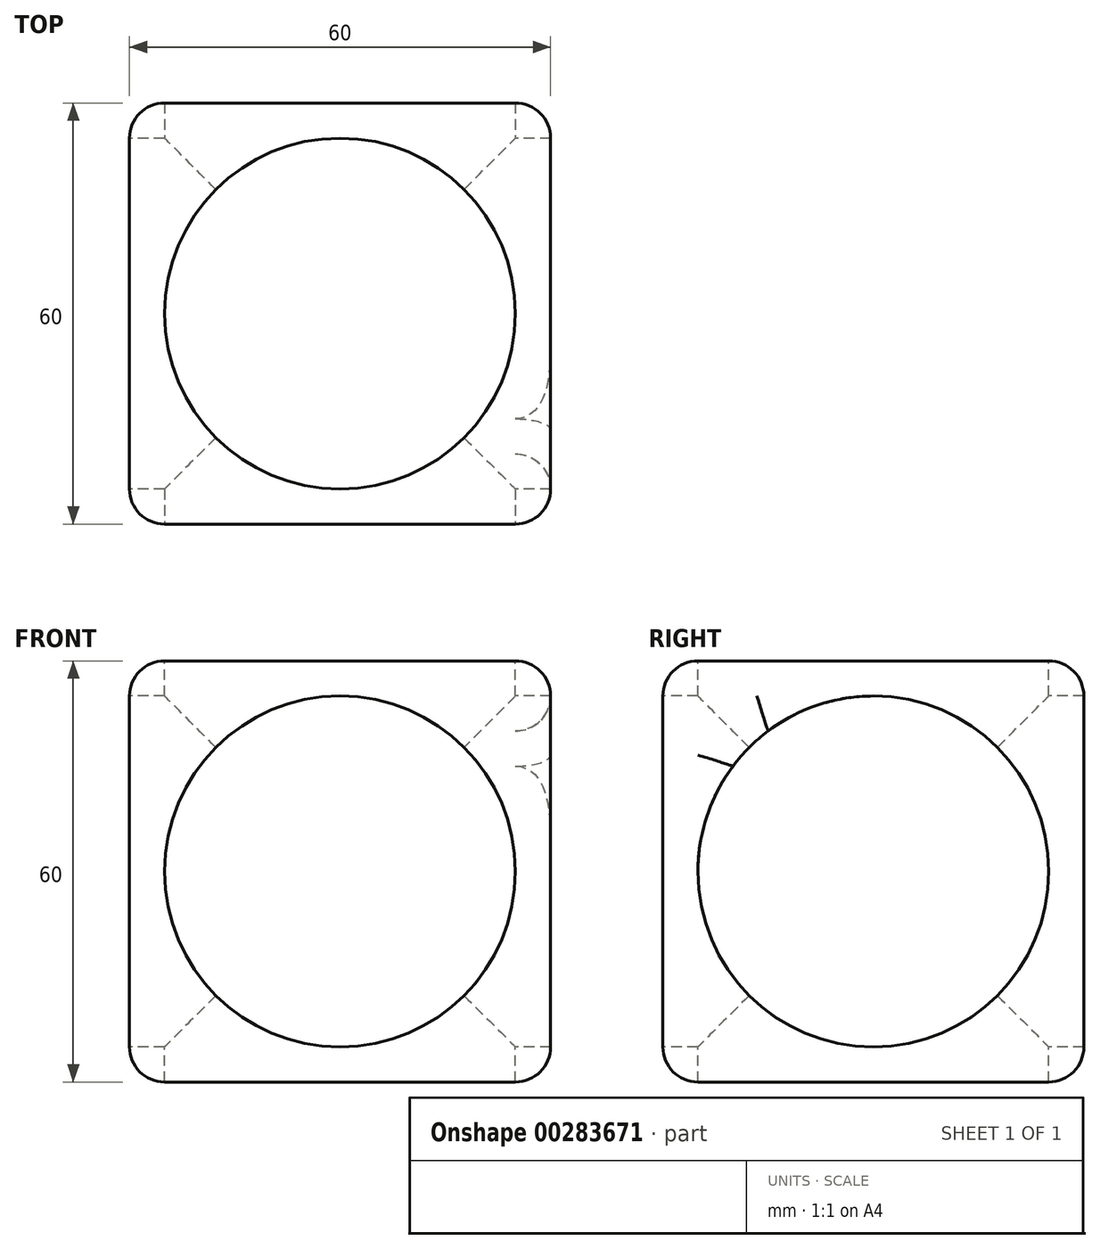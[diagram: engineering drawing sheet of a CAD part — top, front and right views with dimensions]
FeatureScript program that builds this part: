
annotation { "Feature Type Name" : "Feature", "Feature Type Description" : "" }
export const myFeature = defineFeature(function(context is Context, id is Id, definition is map)
    precondition{}
    {
        {
            var Q0;
            Q0=qCreatedBy(makeId("Top.planeOp"),FACE);
            var sketch = newSketch(context, id + "F0", { "sketchPlane" : qUnion([Q0])});
            skLineSegment(sketch, "E0.bottom", {"start": v(30, 30) * mm, "end": v(-30, 30) * mm});
            skLineSegment(sketch, "E0.top", {"start": v(30, -30) * mm, "end": v(-30, -30) * mm});
            skLineSegment(sketch, "E0.left", {"start": v(30, 30) * mm, "end": v(30, -30) * mm});
            skLineSegment(sketch, "E0.right", {"start": v(-30, 30) * mm, "end": v(-30, -30) * mm});
            skPoint(sketch, "E0.middle", {"position": v(0, 0) * mm});
            skSolve(sketch);
        }
        {
            var Q0;
            Q0=makeQuery(id+"F0.imprint","IMPRINT",FACE,{"disambiguationData":[TD([[makeQuery(id+"F0.imprint","IMPRINT",EDGE,{"derivedFrom":sQuery(id+"F0.wireOp",EDGE,"E0.bottom")}),1.0]])]});
            extrude(context, id + "F1", {"entities" : qUnion([Q0]), "depth" : 60 * mm});
        }
        {
            var Q0;
            Q0=makeQuery(id+"F1.opExtrude","CAP_FACE",FACE,{"disambiguationData":[OSD([sQuery(id+"F0.wireOp",EDGE,"E0.bottom"),sQuery(id+"F0.wireOp",EDGE,"E0.top"),sQuery(id+"F0.wireOp",EDGE,"E0.left"),sQuery(id+"F0.wireOp",EDGE,"E0.right")])],"isStart":false});
            var sketch = newSketch(context, id + "F2", { "sketchPlane" : qUnion([Q0])});
            skCircle(sketch, "E1", {"center": v(0, 0) * mm, "radius": 25 * mm});
            skSolve(sketch);
        }
        {
            var Q0;
            Q0=sQuery(id+"F2.wireOp",VERTEX,"E1.center");
            var Q1;
            Q1=makeQuery(id+"F1.opExtrude","SWEPT_BODY",BODY,{"disambiguationData":[OSD([sQuery(id+"F0.wireOp",EDGE,"E0.bottom"),sQuery(id+"F0.wireOp",EDGE,"E0.top"),sQuery(id+"F0.wireOp",EDGE,"E0.left"),sQuery(id+"F0.wireOp",EDGE,"E0.right")])]});
            hole(context, id + "F3", {"style" : HoleStyle.SIMPLE, "endStyle" : HoleEndStyle.THROUGH, "holeDiameter" : 50 * mm, "tappedDepth" : 12 * mm, "tapClearance" : 3, "locations" : qUnion([Q0]), "scope" : qUnion([Q1])});
        }
        {
            var Q0;
            Q0=makeQuery(id+"F1.opExtrude","SWEPT_FACE",FACE,{"disambiguationData":[OSD([sQuery(id+"F0.wireOp",EDGE,"E0.right")])]});
            var sketch = newSketch(context, id + "F4", { "sketchPlane" : qUnion([Q0])});
            skCircle(sketch, "E2", {"center": v(0, 30) * mm, "radius": 30 * mm});
            skPoint(sketch, "E2.first.point", {"position": v(0, 60) * mm});
            skPoint(sketch, "E2.second.point", {"position": v(30, 30) * mm});
            skPoint(sketch, "E2.third.point", {"position": v(-30, 30) * mm});
            skSolve(sketch);
        }
        {
            var Q0;
            Q0=sQuery(id+"F4.wireOp",VERTEX,"E2.center");
            var Q1;
            Q1=makeQuery(id+"F1.opExtrude","SWEPT_BODY",BODY,{"disambiguationData":[OSD([sQuery(id+"F0.wireOp",EDGE,"E0.bottom"),sQuery(id+"F0.wireOp",EDGE,"E0.top"),sQuery(id+"F0.wireOp",EDGE,"E0.left"),sQuery(id+"F0.wireOp",EDGE,"E0.right")])]});
            hole(context, id + "F5", {"style" : HoleStyle.SIMPLE, "endStyle" : HoleEndStyle.THROUGH, "holeDiameter" : 50 * mm, "tappedDepth" : 12 * mm, "tapClearance" : 3, "locations" : qUnion([Q0]), "scope" : qUnion([Q1])});
        }
        {
            var Q0;
            Q0=makeQuery(id+"F1.opExtrude","SWEPT_FACE",FACE,{"disambiguationData":[OSD([sQuery(id+"F0.wireOp",EDGE,"E0.top")])]});
            var sketch = newSketch(context, id + "F6", { "sketchPlane" : qUnion([Q0])});
            skCircle(sketch, "E3", {"center": v(0, 30) * mm, "radius": 30 * mm});
            skPoint(sketch, "E3.first.point", {"position": v(0, 60) * mm});
            skPoint(sketch, "E3.second.point", {"position": v(30, 30) * mm});
            skPoint(sketch, "E3.third.point", {"position": v(-30, 30) * mm});
            skSolve(sketch);
        }
        {
            var Q0;
            Q0=sQuery(id+"F6.wireOp",VERTEX,"E3.center");
            var Q1;
            Q1=makeQuery(id+"F1.opExtrude","SWEPT_BODY",BODY,{"disambiguationData":[OSD([sQuery(id+"F0.wireOp",EDGE,"E0.bottom"),sQuery(id+"F0.wireOp",EDGE,"E0.top"),sQuery(id+"F0.wireOp",EDGE,"E0.left"),sQuery(id+"F0.wireOp",EDGE,"E0.right")])]});
            hole(context, id + "F7", {"style" : HoleStyle.SIMPLE, "endStyle" : HoleEndStyle.THROUGH, "holeDiameter" : 50 * mm, "tappedDepth" : 12 * mm, "tapClearance" : 3, "locations" : qUnion([Q0]), "scope" : qUnion([Q1])});
        }
        {
            var Q0;
            Q0=makeQuery(id+"F1.opExtrude","CAP_EDGE",EDGE,{"disambiguationData":[OSD([sQuery(id+"F0.wireOp",EDGE,"E0.bottom")])],"isStart":false});
            var Q1;
            Q1=makeQuery(id+"F1.opExtrude","CAP_EDGE",EDGE,{"disambiguationData":[OSD([sQuery(id+"F0.wireOp",EDGE,"E0.left")])],"isStart":false});
            var Q2;
            Q2=makeQuery(id+"F1.opExtrude","SWEPT_EDGE",EDGE,{"disambiguationData":[OSD([sQuery(id+"F0.wireOp",EDGE,"E0.bottom"),sQuery(id+"F0.wireOp",EDGE,"E0.left")])]});
            var Q3;
            Q3=makeQuery(id+"F1.opExtrude","CAP_EDGE",EDGE,{"disambiguationData":[OSD([sQuery(id+"F0.wireOp",EDGE,"E0.bottom")])],"isStart":true});
            var Q4;
            Q4=makeQuery(id+"F1.opExtrude","CAP_EDGE",EDGE,{"disambiguationData":[OSD([sQuery(id+"F0.wireOp",EDGE,"E0.left")])],"isStart":true});
            var Q5;
            Q5=makeQuery(id+"F1.opExtrude","SWEPT_EDGE",EDGE,{"disambiguationData":[OSD([sQuery(id+"F0.wireOp",EDGE,"E0.top"),sQuery(id+"F0.wireOp",EDGE,"E0.left")])]});
            var Q6;
            Q6=makeQuery(id+"F1.opExtrude","CAP_EDGE",EDGE,{"disambiguationData":[OSD([sQuery(id+"F0.wireOp",EDGE,"E0.right")])],"isStart":true});
            var Q7;
            Q7=makeQuery(id+"F1.opExtrude","CAP_EDGE",EDGE,{"disambiguationData":[OSD([sQuery(id+"F0.wireOp",EDGE,"E0.top")])],"isStart":true});
            var Q8;
            Q8=makeQuery(id+"F1.opExtrude","SWEPT_EDGE",EDGE,{"disambiguationData":[OSD([sQuery(id+"F0.wireOp",EDGE,"E0.top"),sQuery(id+"F0.wireOp",EDGE,"E0.right")])]});
            var Q9;
            Q9=makeQuery(id+"F1.opExtrude","CAP_EDGE",EDGE,{"disambiguationData":[OSD([sQuery(id+"F0.wireOp",EDGE,"E0.top")])],"isStart":false});
            var Q10;
            Q10=makeQuery(id+"F1.opExtrude","CAP_EDGE",EDGE,{"disambiguationData":[OSD([sQuery(id+"F0.wireOp",EDGE,"E0.right")])],"isStart":false});
            var Q11;
            Q11=makeQuery(id+"F1.opExtrude","SWEPT_EDGE",EDGE,{"disambiguationData":[OSD([sQuery(id+"F0.wireOp",EDGE,"E0.bottom"),sQuery(id+"F0.wireOp",EDGE,"E0.right")])]});
            fillet(context, id + "F8", {"entities" : qUnion([Q0, Q1, Q2, Q3, Q4, Q5, Q6, Q7, Q8, Q9, Q10, Q11]), "radius" : 5 * mm, "tangentPropagation" : true, "allowEdgeOverflow" : false});
        }
        {
            var Q0;
            Q0=makeQuery(id+"F5.hole-0.boolean.opBoolean","INTERSECT",EDGE,{"derivedFrom":[makeQuery(id+"F1.opExtrude","SWEPT_FACE",FACE,{"disambiguationData":[OSD([sQuery(id+"F0.wireOp",EDGE,"E0.left")])]}),makeQuery(id+"F5.hole-0.opRevolve","SWEPT_FACE",FACE,{"disambiguationData":[OSD([sQuery(id+"F5.hole-0.sketch.wireOp",EDGE,"core_line_2")])]})]});
            var Q1;
            Q1=makeQuery(id+"F5.hole-0.boolean.opBoolean","INTERSECT",EDGE,{"derivedFrom":[makeQuery(id+"F1.opExtrude","SWEPT_FACE",FACE,{"disambiguationData":[OSD([sQuery(id+"F0.wireOp",EDGE,"E0.left")])]}),makeQuery(id+"F5.hole-0.opRevolve","SWEPT_FACE",FACE,{"disambiguationData":[OSD([sQuery(id+"F5.hole-0.sketch.wireOp",EDGE,"core_line_2")])]})]});
            var Q2;
            Q2=makeQuery(id+"F5.hole-0.boolean.opBoolean","INTERSECT",EDGE,{"derivedFrom":[makeQuery(id+"F1.opExtrude","SWEPT_FACE",FACE,{"disambiguationData":[OSD([sQuery(id+"F0.wireOp",EDGE,"E0.left")])]}),makeQuery(id+"F5.hole-0.opRevolve","SWEPT_FACE",FACE,{"disambiguationData":[OSD([sQuery(id+"F5.hole-0.sketch.wireOp",EDGE,"core_line_2")])]})]});
            var Q3;
            Q3=makeQuery(id+"F5.hole-0.boolean.opBoolean","INTERSECT",EDGE,{"derivedFrom":[makeQuery(id+"F1.opExtrude","SWEPT_FACE",FACE,{"disambiguationData":[OSD([sQuery(id+"F0.wireOp",EDGE,"E0.left")])]}),makeQuery(id+"F5.hole-0.opRevolve","SWEPT_FACE",FACE,{"disambiguationData":[OSD([sQuery(id+"F5.hole-0.sketch.wireOp",EDGE,"core_line_2")])]})]});
            var Q4;
            Q4=makeQuery(id+"F5.hole-0.boolean.opBoolean","INTERSECT",EDGE,{"derivedFrom":[makeQuery(id+"F1.opExtrude","SWEPT_FACE",FACE,{"disambiguationData":[OSD([sQuery(id+"F0.wireOp",EDGE,"E0.left")])]}),makeQuery(id+"F5.hole-0.opRevolve","SWEPT_FACE",FACE,{"disambiguationData":[OSD([sQuery(id+"F5.hole-0.sketch.wireOp",EDGE,"core_line_2")])]})]});
            var Q5;
            Q5=makeQuery(id+"F5.hole-0.boolean.opBoolean","INTERSECT",EDGE,{"derivedFrom":[makeQuery(id+"F1.opExtrude","SWEPT_FACE",FACE,{"disambiguationData":[OSD([sQuery(id+"F0.wireOp",EDGE,"E0.left")])]}),makeQuery(id+"F5.hole-0.opRevolve","SWEPT_FACE",FACE,{"disambiguationData":[OSD([sQuery(id+"F5.hole-0.sketch.wireOp",EDGE,"core_line_2")])]})]});
            var Q6;
            Q6=makeQuery(id+"F5.hole-0.boolean.opBoolean","INTERSECT",EDGE,{"derivedFrom":[makeQuery(id+"F1.opExtrude","SWEPT_FACE",FACE,{"disambiguationData":[OSD([sQuery(id+"F0.wireOp",EDGE,"E0.left")])]}),makeQuery(id+"F5.hole-0.opRevolve","SWEPT_FACE",FACE,{"disambiguationData":[OSD([sQuery(id+"F5.hole-0.sketch.wireOp",EDGE,"core_line_2")])]})]});
            var Q7;
            Q7=makeQuery(id+"F5.hole-0.boolean.opBoolean","INTERSECT",EDGE,{"derivedFrom":[makeQuery(id+"F1.opExtrude","SWEPT_FACE",FACE,{"disambiguationData":[OSD([sQuery(id+"F0.wireOp",EDGE,"E0.left")])]}),makeQuery(id+"F5.hole-0.opRevolve","SWEPT_FACE",FACE,{"disambiguationData":[OSD([sQuery(id+"F5.hole-0.sketch.wireOp",EDGE,"core_line_2")])]})]});
            var Q8;
            Q8=makeQuery(id+"F5.hole-0.boolean.opBoolean","INTERSECT",EDGE,{"derivedFrom":[makeQuery(id+"F1.opExtrude","SWEPT_FACE",FACE,{"disambiguationData":[OSD([sQuery(id+"F0.wireOp",EDGE,"E0.left")])]}),makeQuery(id+"F5.hole-0.opRevolve","SWEPT_FACE",FACE,{"disambiguationData":[OSD([sQuery(id+"F5.hole-0.sketch.wireOp",EDGE,"core_line_2")])]})]});
            var Q9;
            Q9=makeQuery(id+"F5.hole-0.boolean.opBoolean","INTERSECT",EDGE,{"derivedFrom":[makeQuery(id+"F1.opExtrude","SWEPT_FACE",FACE,{"disambiguationData":[OSD([sQuery(id+"F0.wireOp",EDGE,"E0.left")])]}),makeQuery(id+"F5.hole-0.opRevolve","SWEPT_FACE",FACE,{"disambiguationData":[OSD([sQuery(id+"F5.hole-0.sketch.wireOp",EDGE,"core_line_2")])]})]});
            var Q10;
            Q10=makeQuery(id+"F5.hole-0.boolean.opBoolean","INTERSECT",EDGE,{"derivedFrom":[makeQuery(id+"F1.opExtrude","SWEPT_FACE",FACE,{"disambiguationData":[OSD([sQuery(id+"F0.wireOp",EDGE,"E0.left")])]}),makeQuery(id+"F5.hole-0.opRevolve","SWEPT_FACE",FACE,{"disambiguationData":[OSD([sQuery(id+"F5.hole-0.sketch.wireOp",EDGE,"core_line_2")])]})]});
            var Q11;
            Q11=makeQuery(id+"F5.hole-0.boolean.opBoolean","INTERSECT",EDGE,{"derivedFrom":[makeQuery(id+"F1.opExtrude","SWEPT_FACE",FACE,{"disambiguationData":[OSD([sQuery(id+"F0.wireOp",EDGE,"E0.left")])]}),makeQuery(id+"F5.hole-0.opRevolve","SWEPT_FACE",FACE,{"disambiguationData":[OSD([sQuery(id+"F5.hole-0.sketch.wireOp",EDGE,"core_line_2")])]})]});
            var Q12;
            Q12=makeQuery(id+"F5.hole-0.boolean.opBoolean","INTERSECT",EDGE,{"derivedFrom":[makeQuery(id+"F1.opExtrude","SWEPT_FACE",FACE,{"disambiguationData":[OSD([sQuery(id+"F0.wireOp",EDGE,"E0.left")])]}),makeQuery(id+"F5.hole-0.opRevolve","SWEPT_FACE",FACE,{"disambiguationData":[OSD([sQuery(id+"F5.hole-0.sketch.wireOp",EDGE,"core_line_2")])]})]});
            var Q13;
            Q13=makeQuery(id+"F5.hole-0.boolean.opBoolean","INTERSECT",EDGE,{"derivedFrom":[makeQuery(id+"F1.opExtrude","SWEPT_FACE",FACE,{"disambiguationData":[OSD([sQuery(id+"F0.wireOp",EDGE,"E0.left")])]}),makeQuery(id+"F5.hole-0.opRevolve","SWEPT_FACE",FACE,{"disambiguationData":[OSD([sQuery(id+"F5.hole-0.sketch.wireOp",EDGE,"core_line_2")])]})]});
            var Q14;
            Q14=makeQuery(id+"F5.hole-0.boolean.opBoolean","INTERSECT",EDGE,{"derivedFrom":[makeQuery(id+"F1.opExtrude","SWEPT_FACE",FACE,{"disambiguationData":[OSD([sQuery(id+"F0.wireOp",EDGE,"E0.left")])]}),makeQuery(id+"F5.hole-0.opRevolve","SWEPT_FACE",FACE,{"disambiguationData":[OSD([sQuery(id+"F5.hole-0.sketch.wireOp",EDGE,"core_line_2")])]})]});
            var Q15;
            Q15=makeQuery(id+"F5.hole-0.boolean.opBoolean","INTERSECT",EDGE,{"derivedFrom":[makeQuery(id+"F1.opExtrude","SWEPT_FACE",FACE,{"disambiguationData":[OSD([sQuery(id+"F0.wireOp",EDGE,"E0.left")])]}),makeQuery(id+"F5.hole-0.opRevolve","SWEPT_FACE",FACE,{"disambiguationData":[OSD([sQuery(id+"F5.hole-0.sketch.wireOp",EDGE,"core_line_2")])]})]});
            var Q16;
            Q16=makeQuery(id+"F5.hole-0.boolean.opBoolean","INTERSECT",EDGE,{"derivedFrom":[makeQuery(id+"F1.opExtrude","SWEPT_FACE",FACE,{"disambiguationData":[OSD([sQuery(id+"F0.wireOp",EDGE,"E0.left")])]}),makeQuery(id+"F5.hole-0.opRevolve","SWEPT_FACE",FACE,{"disambiguationData":[OSD([sQuery(id+"F5.hole-0.sketch.wireOp",EDGE,"core_line_2")])]})]});
            var Q17;
            Q17=makeQuery(id+"F5.hole-0.boolean.opBoolean","INTERSECT",EDGE,{"derivedFrom":[makeQuery(id+"F1.opExtrude","SWEPT_FACE",FACE,{"disambiguationData":[OSD([sQuery(id+"F0.wireOp",EDGE,"E0.left")])]}),makeQuery(id+"F5.hole-0.opRevolve","SWEPT_FACE",FACE,{"disambiguationData":[OSD([sQuery(id+"F5.hole-0.sketch.wireOp",EDGE,"core_line_2")])]})]});
            var Q18;
            Q18=makeQuery(id+"F5.hole-0.boolean.opBoolean","INTERSECT",EDGE,{"derivedFrom":[makeQuery(id+"F1.opExtrude","SWEPT_FACE",FACE,{"disambiguationData":[OSD([sQuery(id+"F0.wireOp",EDGE,"E0.left")])]}),makeQuery(id+"F5.hole-0.opRevolve","SWEPT_FACE",FACE,{"disambiguationData":[OSD([sQuery(id+"F5.hole-0.sketch.wireOp",EDGE,"core_line_2")])]})]});
            var Q19;
            Q19=makeQuery(id+"F5.hole-0.boolean.opBoolean","INTERSECT",EDGE,{"derivedFrom":[makeQuery(id+"F1.opExtrude","SWEPT_FACE",FACE,{"disambiguationData":[OSD([sQuery(id+"F0.wireOp",EDGE,"E0.left")])]}),makeQuery(id+"F5.hole-0.opRevolve","SWEPT_FACE",FACE,{"disambiguationData":[OSD([sQuery(id+"F5.hole-0.sketch.wireOp",EDGE,"core_line_2")])]})]});
            var Q20;
            Q20=makeQuery(id+"F5.hole-0.boolean.opBoolean","INTERSECT",EDGE,{"derivedFrom":[makeQuery(id+"F1.opExtrude","SWEPT_FACE",FACE,{"disambiguationData":[OSD([sQuery(id+"F0.wireOp",EDGE,"E0.left")])]}),makeQuery(id+"F5.hole-0.opRevolve","SWEPT_FACE",FACE,{"disambiguationData":[OSD([sQuery(id+"F5.hole-0.sketch.wireOp",EDGE,"core_line_2")])]})]});
            var Q21;
            Q21=makeQuery(id+"F5.hole-0.boolean.opBoolean","INTERSECT",EDGE,{"derivedFrom":[makeQuery(id+"F1.opExtrude","SWEPT_FACE",FACE,{"disambiguationData":[OSD([sQuery(id+"F0.wireOp",EDGE,"E0.left")])]}),makeQuery(id+"F5.hole-0.opRevolve","SWEPT_FACE",FACE,{"disambiguationData":[OSD([sQuery(id+"F5.hole-0.sketch.wireOp",EDGE,"core_line_2")])]})]});
            var Q22;
            Q22=makeQuery(id+"F5.hole-0.boolean.opBoolean","INTERSECT",EDGE,{"derivedFrom":[makeQuery(id+"F1.opExtrude","SWEPT_FACE",FACE,{"disambiguationData":[OSD([sQuery(id+"F0.wireOp",EDGE,"E0.left")])]}),makeQuery(id+"F5.hole-0.opRevolve","SWEPT_FACE",FACE,{"disambiguationData":[OSD([sQuery(id+"F5.hole-0.sketch.wireOp",EDGE,"core_line_2")])]})]});
            var Q23;
            Q23=makeQuery(id+"F5.hole-0.boolean.opBoolean","INTERSECT",EDGE,{"derivedFrom":[makeQuery(id+"F1.opExtrude","SWEPT_FACE",FACE,{"disambiguationData":[OSD([sQuery(id+"F0.wireOp",EDGE,"E0.left")])]}),makeQuery(id+"F5.hole-0.opRevolve","SWEPT_FACE",FACE,{"disambiguationData":[OSD([sQuery(id+"F5.hole-0.sketch.wireOp",EDGE,"core_line_2")])]})]});
            var Q24;
            Q24=makeQuery(id+"F5.hole-0.boolean.opBoolean","INTERSECT",EDGE,{"derivedFrom":[makeQuery(id+"F1.opExtrude","SWEPT_FACE",FACE,{"disambiguationData":[OSD([sQuery(id+"F0.wireOp",EDGE,"E0.left")])]}),makeQuery(id+"F5.hole-0.opRevolve","SWEPT_FACE",FACE,{"disambiguationData":[OSD([sQuery(id+"F5.hole-0.sketch.wireOp",EDGE,"core_line_2")])]})]});
            var Q25;
            Q25=makeQuery(id+"F5.hole-0.boolean.opBoolean","INTERSECT",EDGE,{"derivedFrom":[makeQuery(id+"F1.opExtrude","SWEPT_FACE",FACE,{"disambiguationData":[OSD([sQuery(id+"F0.wireOp",EDGE,"E0.left")])]}),makeQuery(id+"F5.hole-0.opRevolve","SWEPT_FACE",FACE,{"disambiguationData":[OSD([sQuery(id+"F5.hole-0.sketch.wireOp",EDGE,"core_line_2")])]})]});
            var Q26;
            Q26=makeQuery(id+"F5.hole-0.boolean.opBoolean","INTERSECT",EDGE,{"derivedFrom":[makeQuery(id+"F1.opExtrude","SWEPT_FACE",FACE,{"disambiguationData":[OSD([sQuery(id+"F0.wireOp",EDGE,"E0.left")])]}),makeQuery(id+"F5.hole-0.opRevolve","SWEPT_FACE",FACE,{"disambiguationData":[OSD([sQuery(id+"F5.hole-0.sketch.wireOp",EDGE,"core_line_2")])]})]});
            var Q27;
            Q27=makeQuery(id+"F5.hole-0.boolean.opBoolean","INTERSECT",EDGE,{"derivedFrom":[makeQuery(id+"F1.opExtrude","SWEPT_FACE",FACE,{"disambiguationData":[OSD([sQuery(id+"F0.wireOp",EDGE,"E0.left")])]}),makeQuery(id+"F5.hole-0.opRevolve","SWEPT_FACE",FACE,{"disambiguationData":[OSD([sQuery(id+"F5.hole-0.sketch.wireOp",EDGE,"core_line_2")])]})]});
            var Q28;
            Q28=makeQuery(id+"F5.hole-0.boolean.opBoolean","INTERSECT",EDGE,{"derivedFrom":[makeQuery(id+"F1.opExtrude","SWEPT_FACE",FACE,{"disambiguationData":[OSD([sQuery(id+"F0.wireOp",EDGE,"E0.left")])]}),makeQuery(id+"F5.hole-0.opRevolve","SWEPT_FACE",FACE,{"disambiguationData":[OSD([sQuery(id+"F5.hole-0.sketch.wireOp",EDGE,"core_line_2")])]})]});
            var Q29;
            Q29=makeQuery(id+"F5.hole-0.boolean.opBoolean","INTERSECT",EDGE,{"derivedFrom":[makeQuery(id+"F1.opExtrude","SWEPT_FACE",FACE,{"disambiguationData":[OSD([sQuery(id+"F0.wireOp",EDGE,"E0.left")])]}),makeQuery(id+"F5.hole-0.opRevolve","SWEPT_FACE",FACE,{"disambiguationData":[OSD([sQuery(id+"F5.hole-0.sketch.wireOp",EDGE,"core_line_2")])]})]});
            var Q30;
            Q30=makeQuery(id+"F5.hole-0.boolean.opBoolean","INTERSECT",EDGE,{"derivedFrom":[makeQuery(id+"F1.opExtrude","SWEPT_FACE",FACE,{"disambiguationData":[OSD([sQuery(id+"F0.wireOp",EDGE,"E0.left")])]}),makeQuery(id+"F5.hole-0.opRevolve","SWEPT_FACE",FACE,{"disambiguationData":[OSD([sQuery(id+"F5.hole-0.sketch.wireOp",EDGE,"core_line_2")])]})]});
            var Q31;
            Q31=makeQuery(id+"F5.hole-0.boolean.opBoolean","INTERSECT",EDGE,{"derivedFrom":[makeQuery(id+"F1.opExtrude","SWEPT_FACE",FACE,{"disambiguationData":[OSD([sQuery(id+"F0.wireOp",EDGE,"E0.left")])]}),makeQuery(id+"F5.hole-0.opRevolve","SWEPT_FACE",FACE,{"disambiguationData":[OSD([sQuery(id+"F5.hole-0.sketch.wireOp",EDGE,"core_line_2")])]})]});
            var Q32;
            Q32=makeQuery(id+"F5.hole-0.boolean.opBoolean","INTERSECT",EDGE,{"derivedFrom":[makeQuery(id+"F1.opExtrude","SWEPT_FACE",FACE,{"disambiguationData":[OSD([sQuery(id+"F0.wireOp",EDGE,"E0.left")])]}),makeQuery(id+"F5.hole-0.opRevolve","SWEPT_FACE",FACE,{"disambiguationData":[OSD([sQuery(id+"F5.hole-0.sketch.wireOp",EDGE,"core_line_2")])]})]});
            var Q33;
            Q33=makeQuery(id+"F5.hole-0.boolean.opBoolean","INTERSECT",EDGE,{"derivedFrom":[makeQuery(id+"F1.opExtrude","SWEPT_FACE",FACE,{"disambiguationData":[OSD([sQuery(id+"F0.wireOp",EDGE,"E0.left")])]}),makeQuery(id+"F5.hole-0.opRevolve","SWEPT_FACE",FACE,{"disambiguationData":[OSD([sQuery(id+"F5.hole-0.sketch.wireOp",EDGE,"core_line_2")])]})]});
            var Q34;
            Q34=makeQuery(id+"F5.hole-0.boolean.opBoolean","INTERSECT",EDGE,{"derivedFrom":[makeQuery(id+"F1.opExtrude","SWEPT_FACE",FACE,{"disambiguationData":[OSD([sQuery(id+"F0.wireOp",EDGE,"E0.left")])]}),makeQuery(id+"F5.hole-0.opRevolve","SWEPT_FACE",FACE,{"disambiguationData":[OSD([sQuery(id+"F5.hole-0.sketch.wireOp",EDGE,"core_line_2")])]})]});
            var Q35;
            Q35=makeQuery(id+"F5.hole-0.boolean.opBoolean","INTERSECT",EDGE,{"derivedFrom":[makeQuery(id+"F1.opExtrude","SWEPT_FACE",FACE,{"disambiguationData":[OSD([sQuery(id+"F0.wireOp",EDGE,"E0.left")])]}),makeQuery(id+"F5.hole-0.opRevolve","SWEPT_FACE",FACE,{"disambiguationData":[OSD([sQuery(id+"F5.hole-0.sketch.wireOp",EDGE,"core_line_2")])]})]});
            var Q36;
            Q36=makeQuery(id+"F5.hole-0.boolean.opBoolean","COPY",EDGE,{"derivedFrom":makeQuery(id+"F5.hole-0.opRevolve","SWEPT_EDGE",EDGE,{"disambiguationData":[OSD([sQuery(id+"F5.hole-0.sketch.wireOp",EDGE,"core_line_2"),sQuery(id+"F5.hole-0.sketch.wireOp",EDGE,"core_line_3")])]})});
            var Q37;
            Q37=makeQuery(id+"F5.hole-0.boolean.opBoolean","COPY",EDGE,{"derivedFrom":makeQuery(id+"F5.hole-0.opRevolve","SWEPT_EDGE",EDGE,{"disambiguationData":[OSD([sQuery(id+"F5.hole-0.sketch.wireOp",EDGE,"core_line_2"),sQuery(id+"F5.hole-0.sketch.wireOp",EDGE,"core_line_3")])]})});
            var Q38;
            Q38=makeQuery(id+"F5.hole-0.boolean.opBoolean","COPY",EDGE,{"derivedFrom":makeQuery(id+"F5.hole-0.opRevolve","SWEPT_EDGE",EDGE,{"disambiguationData":[OSD([sQuery(id+"F5.hole-0.sketch.wireOp",EDGE,"core_line_2"),sQuery(id+"F5.hole-0.sketch.wireOp",EDGE,"core_line_3")])]})});
            var Q39;
            Q39=makeQuery(id+"F5.hole-0.boolean.opBoolean","COPY",EDGE,{"derivedFrom":makeQuery(id+"F5.hole-0.opRevolve","SWEPT_EDGE",EDGE,{"disambiguationData":[OSD([sQuery(id+"F5.hole-0.sketch.wireOp",EDGE,"core_line_2"),sQuery(id+"F5.hole-0.sketch.wireOp",EDGE,"core_line_3")])]})});
            var Q40;
            Q40=makeQuery(id+"F5.hole-0.boolean.opBoolean","COPY",EDGE,{"derivedFrom":makeQuery(id+"F5.hole-0.opRevolve","SWEPT_EDGE",EDGE,{"disambiguationData":[OSD([sQuery(id+"F5.hole-0.sketch.wireOp",EDGE,"core_line_2"),sQuery(id+"F5.hole-0.sketch.wireOp",EDGE,"core_line_3")])]})});
            var Q41;
            Q41=makeQuery(id+"F5.hole-0.boolean.opBoolean","COPY",EDGE,{"derivedFrom":makeQuery(id+"F5.hole-0.opRevolve","SWEPT_EDGE",EDGE,{"disambiguationData":[OSD([sQuery(id+"F5.hole-0.sketch.wireOp",EDGE,"core_line_2"),sQuery(id+"F5.hole-0.sketch.wireOp",EDGE,"core_line_3")])]})});
            var Q42;
            Q42=makeQuery(id+"F5.hole-0.boolean.opBoolean","COPY",EDGE,{"derivedFrom":makeQuery(id+"F5.hole-0.opRevolve","SWEPT_EDGE",EDGE,{"disambiguationData":[OSD([sQuery(id+"F5.hole-0.sketch.wireOp",EDGE,"core_line_2"),sQuery(id+"F5.hole-0.sketch.wireOp",EDGE,"core_line_3")])]})});
            var Q43;
            Q43=makeQuery(id+"F5.hole-0.boolean.opBoolean","COPY",EDGE,{"derivedFrom":makeQuery(id+"F5.hole-0.opRevolve","SWEPT_EDGE",EDGE,{"disambiguationData":[OSD([sQuery(id+"F5.hole-0.sketch.wireOp",EDGE,"core_line_2"),sQuery(id+"F5.hole-0.sketch.wireOp",EDGE,"core_line_3")])]})});
            var Q44;
            Q44=makeQuery(id+"F5.hole-0.boolean.opBoolean","COPY",EDGE,{"derivedFrom":makeQuery(id+"F5.hole-0.opRevolve","SWEPT_EDGE",EDGE,{"disambiguationData":[OSD([sQuery(id+"F5.hole-0.sketch.wireOp",EDGE,"core_line_2"),sQuery(id+"F5.hole-0.sketch.wireOp",EDGE,"core_line_3")])]})});
            var Q45;
            Q45=makeQuery(id+"F5.hole-0.boolean.opBoolean","COPY",EDGE,{"derivedFrom":makeQuery(id+"F5.hole-0.opRevolve","SWEPT_EDGE",EDGE,{"disambiguationData":[OSD([sQuery(id+"F5.hole-0.sketch.wireOp",EDGE,"core_line_2"),sQuery(id+"F5.hole-0.sketch.wireOp",EDGE,"core_line_3")])]})});
            var Q46;
            Q46=makeQuery(id+"F5.hole-0.boolean.opBoolean","COPY",EDGE,{"derivedFrom":makeQuery(id+"F5.hole-0.opRevolve","SWEPT_EDGE",EDGE,{"disambiguationData":[OSD([sQuery(id+"F5.hole-0.sketch.wireOp",EDGE,"core_line_2"),sQuery(id+"F5.hole-0.sketch.wireOp",EDGE,"core_line_3")])]})});
            var Q47;
            Q47=makeQuery(id+"F5.hole-0.boolean.opBoolean","COPY",EDGE,{"derivedFrom":makeQuery(id+"F5.hole-0.opRevolve","SWEPT_EDGE",EDGE,{"disambiguationData":[OSD([sQuery(id+"F5.hole-0.sketch.wireOp",EDGE,"core_line_2"),sQuery(id+"F5.hole-0.sketch.wireOp",EDGE,"core_line_3")])]})});
            var Q48;
            Q48=makeQuery(id+"F5.hole-0.boolean.opBoolean","INTERSECT",EDGE,{"derivedFrom":[makeQuery(id+"F1.opExtrude","SWEPT_FACE",FACE,{"disambiguationData":[OSD([sQuery(id+"F0.wireOp",EDGE,"E0.left")])]}),makeQuery(id+"F5.hole-0.opRevolve","SWEPT_FACE",FACE,{"disambiguationData":[OSD([sQuery(id+"F5.hole-0.sketch.wireOp",EDGE,"core_line_2")])]})]});
            var Q49;
            Q49=makeQuery(id+"F5.hole-0.boolean.opBoolean","INTERSECT",EDGE,{"derivedFrom":[makeQuery(id+"F1.opExtrude","SWEPT_FACE",FACE,{"disambiguationData":[OSD([sQuery(id+"F0.wireOp",EDGE,"E0.left")])]}),makeQuery(id+"F5.hole-0.opRevolve","SWEPT_FACE",FACE,{"disambiguationData":[OSD([sQuery(id+"F5.hole-0.sketch.wireOp",EDGE,"core_line_2")])]})]});
            var Q50;
            Q50=makeQuery(id+"F5.hole-0.boolean.opBoolean","INTERSECT",EDGE,{"derivedFrom":[makeQuery(id+"F1.opExtrude","SWEPT_FACE",FACE,{"disambiguationData":[OSD([sQuery(id+"F0.wireOp",EDGE,"E0.left")])]}),makeQuery(id+"F5.hole-0.opRevolve","SWEPT_FACE",FACE,{"disambiguationData":[OSD([sQuery(id+"F5.hole-0.sketch.wireOp",EDGE,"core_line_2")])]})]});
            var Q51;
            Q51=makeQuery(id+"F5.hole-0.boolean.opBoolean","INTERSECT",EDGE,{"derivedFrom":[makeQuery(id+"F1.opExtrude","SWEPT_FACE",FACE,{"disambiguationData":[OSD([sQuery(id+"F0.wireOp",EDGE,"E0.left")])]}),makeQuery(id+"F5.hole-0.opRevolve","SWEPT_FACE",FACE,{"disambiguationData":[OSD([sQuery(id+"F5.hole-0.sketch.wireOp",EDGE,"core_line_2")])]})]});
            var Q52;
            Q52=makeQuery(id+"F5.hole-0.boolean.opBoolean","INTERSECT",EDGE,{"derivedFrom":[makeQuery(id+"F1.opExtrude","SWEPT_FACE",FACE,{"disambiguationData":[OSD([sQuery(id+"F0.wireOp",EDGE,"E0.left")])]}),makeQuery(id+"F5.hole-0.opRevolve","SWEPT_FACE",FACE,{"disambiguationData":[OSD([sQuery(id+"F5.hole-0.sketch.wireOp",EDGE,"core_line_2")])]})]});
            var Q53;
            Q53=makeQuery(id+"F5.hole-0.boolean.opBoolean","INTERSECT",EDGE,{"derivedFrom":[makeQuery(id+"F1.opExtrude","SWEPT_FACE",FACE,{"disambiguationData":[OSD([sQuery(id+"F0.wireOp",EDGE,"E0.left")])]}),makeQuery(id+"F5.hole-0.opRevolve","SWEPT_FACE",FACE,{"disambiguationData":[OSD([sQuery(id+"F5.hole-0.sketch.wireOp",EDGE,"core_line_2")])]})]});
            var Q54;
            Q54=makeQuery(id+"F5.hole-0.boolean.opBoolean","INTERSECT",EDGE,{"derivedFrom":[makeQuery(id+"F1.opExtrude","SWEPT_FACE",FACE,{"disambiguationData":[OSD([sQuery(id+"F0.wireOp",EDGE,"E0.left")])]}),makeQuery(id+"F5.hole-0.opRevolve","SWEPT_FACE",FACE,{"disambiguationData":[OSD([sQuery(id+"F5.hole-0.sketch.wireOp",EDGE,"core_line_2")])]})]});
            var Q55;
            Q55=makeQuery(id+"F5.hole-0.boolean.opBoolean","INTERSECT",EDGE,{"derivedFrom":[makeQuery(id+"F1.opExtrude","SWEPT_FACE",FACE,{"disambiguationData":[OSD([sQuery(id+"F0.wireOp",EDGE,"E0.left")])]}),makeQuery(id+"F5.hole-0.opRevolve","SWEPT_FACE",FACE,{"disambiguationData":[OSD([sQuery(id+"F5.hole-0.sketch.wireOp",EDGE,"core_line_2")])]})]});
            var Q56;
            Q56=makeQuery(id+"F5.hole-0.boolean.opBoolean","INTERSECT",EDGE,{"derivedFrom":[makeQuery(id+"F1.opExtrude","SWEPT_FACE",FACE,{"disambiguationData":[OSD([sQuery(id+"F0.wireOp",EDGE,"E0.left")])]}),makeQuery(id+"F5.hole-0.opRevolve","SWEPT_FACE",FACE,{"disambiguationData":[OSD([sQuery(id+"F5.hole-0.sketch.wireOp",EDGE,"core_line_2")])]})]});
            var Q57;
            Q57=makeQuery(id+"F5.hole-0.boolean.opBoolean","INTERSECT",EDGE,{"derivedFrom":[makeQuery(id+"F1.opExtrude","SWEPT_FACE",FACE,{"disambiguationData":[OSD([sQuery(id+"F0.wireOp",EDGE,"E0.left")])]}),makeQuery(id+"F5.hole-0.opRevolve","SWEPT_FACE",FACE,{"disambiguationData":[OSD([sQuery(id+"F5.hole-0.sketch.wireOp",EDGE,"core_line_2")])]})]});
            var Q58;
            Q58=makeQuery(id+"F5.hole-0.boolean.opBoolean","INTERSECT",EDGE,{"derivedFrom":[makeQuery(id+"F1.opExtrude","SWEPT_FACE",FACE,{"disambiguationData":[OSD([sQuery(id+"F0.wireOp",EDGE,"E0.left")])]}),makeQuery(id+"F5.hole-0.opRevolve","SWEPT_FACE",FACE,{"disambiguationData":[OSD([sQuery(id+"F5.hole-0.sketch.wireOp",EDGE,"core_line_2")])]})]});
            var Q59;
            Q59=makeQuery(id+"F5.hole-0.boolean.opBoolean","INTERSECT",EDGE,{"derivedFrom":[makeQuery(id+"F1.opExtrude","SWEPT_FACE",FACE,{"disambiguationData":[OSD([sQuery(id+"F0.wireOp",EDGE,"E0.left")])]}),makeQuery(id+"F5.hole-0.opRevolve","SWEPT_FACE",FACE,{"disambiguationData":[OSD([sQuery(id+"F5.hole-0.sketch.wireOp",EDGE,"core_line_2")])]})]});
            var Q60;
            Q60=makeQuery(id+"F5.hole-0.boolean.opBoolean","INTERSECT",EDGE,{"derivedFrom":[makeQuery(id+"F1.opExtrude","SWEPT_FACE",FACE,{"disambiguationData":[OSD([sQuery(id+"F0.wireOp",EDGE,"E0.left")])]}),makeQuery(id+"F5.hole-0.opRevolve","SWEPT_FACE",FACE,{"disambiguationData":[OSD([sQuery(id+"F5.hole-0.sketch.wireOp",EDGE,"core_line_2")])]})]});
            var Q61;
            Q61=makeQuery(id+"F5.hole-0.boolean.opBoolean","INTERSECT",EDGE,{"derivedFrom":[makeQuery(id+"F1.opExtrude","SWEPT_FACE",FACE,{"disambiguationData":[OSD([sQuery(id+"F0.wireOp",EDGE,"E0.left")])]}),makeQuery(id+"F5.hole-0.opRevolve","SWEPT_FACE",FACE,{"disambiguationData":[OSD([sQuery(id+"F5.hole-0.sketch.wireOp",EDGE,"core_line_2")])]})]});
            var Q62;
            Q62=makeQuery(id+"F5.hole-0.boolean.opBoolean","INTERSECT",EDGE,{"derivedFrom":[makeQuery(id+"F1.opExtrude","SWEPT_FACE",FACE,{"disambiguationData":[OSD([sQuery(id+"F0.wireOp",EDGE,"E0.left")])]}),makeQuery(id+"F5.hole-0.opRevolve","SWEPT_FACE",FACE,{"disambiguationData":[OSD([sQuery(id+"F5.hole-0.sketch.wireOp",EDGE,"core_line_2")])]})]});
            var Q63;
            Q63=makeQuery(id+"F5.hole-0.boolean.opBoolean","INTERSECT",EDGE,{"derivedFrom":[makeQuery(id+"F1.opExtrude","SWEPT_FACE",FACE,{"disambiguationData":[OSD([sQuery(id+"F0.wireOp",EDGE,"E0.left")])]}),makeQuery(id+"F5.hole-0.opRevolve","SWEPT_FACE",FACE,{"disambiguationData":[OSD([sQuery(id+"F5.hole-0.sketch.wireOp",EDGE,"core_line_2")])]})]});
            var Q64;
            Q64=makeQuery(id+"F5.hole-0.boolean.opBoolean","INTERSECT",EDGE,{"derivedFrom":[makeQuery(id+"F1.opExtrude","SWEPT_FACE",FACE,{"disambiguationData":[OSD([sQuery(id+"F0.wireOp",EDGE,"E0.left")])]}),makeQuery(id+"F5.hole-0.opRevolve","SWEPT_FACE",FACE,{"disambiguationData":[OSD([sQuery(id+"F5.hole-0.sketch.wireOp",EDGE,"core_line_2")])]})]});
            var Q65;
            Q65=makeQuery(id+"F5.hole-0.boolean.opBoolean","INTERSECT",EDGE,{"derivedFrom":[makeQuery(id+"F1.opExtrude","SWEPT_FACE",FACE,{"disambiguationData":[OSD([sQuery(id+"F0.wireOp",EDGE,"E0.left")])]}),makeQuery(id+"F5.hole-0.opRevolve","SWEPT_FACE",FACE,{"disambiguationData":[OSD([sQuery(id+"F5.hole-0.sketch.wireOp",EDGE,"core_line_2")])]})]});
            var Q66;
            Q66=makeQuery(id+"F5.hole-0.boolean.opBoolean","INTERSECT",EDGE,{"derivedFrom":[makeQuery(id+"F1.opExtrude","SWEPT_FACE",FACE,{"disambiguationData":[OSD([sQuery(id+"F0.wireOp",EDGE,"E0.left")])]}),makeQuery(id+"F5.hole-0.opRevolve","SWEPT_FACE",FACE,{"disambiguationData":[OSD([sQuery(id+"F5.hole-0.sketch.wireOp",EDGE,"core_line_2")])]})]});
            var Q67;
            Q67=makeQuery(id+"F5.hole-0.boolean.opBoolean","INTERSECT",EDGE,{"derivedFrom":[makeQuery(id+"F1.opExtrude","SWEPT_FACE",FACE,{"disambiguationData":[OSD([sQuery(id+"F0.wireOp",EDGE,"E0.left")])]}),makeQuery(id+"F5.hole-0.opRevolve","SWEPT_FACE",FACE,{"disambiguationData":[OSD([sQuery(id+"F5.hole-0.sketch.wireOp",EDGE,"core_line_2")])]})]});
            var Q68;
            Q68=makeQuery(id+"F5.hole-0.boolean.opBoolean","INTERSECT",EDGE,{"derivedFrom":[makeQuery(id+"F1.opExtrude","SWEPT_FACE",FACE,{"disambiguationData":[OSD([sQuery(id+"F0.wireOp",EDGE,"E0.left")])]}),makeQuery(id+"F5.hole-0.opRevolve","SWEPT_FACE",FACE,{"disambiguationData":[OSD([sQuery(id+"F5.hole-0.sketch.wireOp",EDGE,"core_line_2")])]})]});
            var Q69;
            Q69=makeQuery(id+"F5.hole-0.boolean.opBoolean","INTERSECT",EDGE,{"derivedFrom":[makeQuery(id+"F1.opExtrude","SWEPT_FACE",FACE,{"disambiguationData":[OSD([sQuery(id+"F0.wireOp",EDGE,"E0.left")])]}),makeQuery(id+"F5.hole-0.opRevolve","SWEPT_FACE",FACE,{"disambiguationData":[OSD([sQuery(id+"F5.hole-0.sketch.wireOp",EDGE,"core_line_2")])]})]});
            var Q70;
            Q70=makeQuery(id+"F5.hole-0.boolean.opBoolean","INTERSECT",EDGE,{"derivedFrom":[makeQuery(id+"F1.opExtrude","SWEPT_FACE",FACE,{"disambiguationData":[OSD([sQuery(id+"F0.wireOp",EDGE,"E0.left")])]}),makeQuery(id+"F5.hole-0.opRevolve","SWEPT_FACE",FACE,{"disambiguationData":[OSD([sQuery(id+"F5.hole-0.sketch.wireOp",EDGE,"core_line_2")])]})]});
            var Q71;
            Q71=makeQuery(id+"F5.hole-0.boolean.opBoolean","INTERSECT",EDGE,{"derivedFrom":[makeQuery(id+"F1.opExtrude","SWEPT_FACE",FACE,{"disambiguationData":[OSD([sQuery(id+"F0.wireOp",EDGE,"E0.left")])]}),makeQuery(id+"F5.hole-0.opRevolve","SWEPT_FACE",FACE,{"disambiguationData":[OSD([sQuery(id+"F5.hole-0.sketch.wireOp",EDGE,"core_line_2")])]})]});
            var Q72;
            Q72=makeQuery(id+"F5.hole-0.boolean.opBoolean","INTERSECT",EDGE,{"derivedFrom":[makeQuery(id+"F1.opExtrude","SWEPT_FACE",FACE,{"disambiguationData":[OSD([sQuery(id+"F0.wireOp",EDGE,"E0.left")])]}),makeQuery(id+"F5.hole-0.opRevolve","SWEPT_FACE",FACE,{"disambiguationData":[OSD([sQuery(id+"F5.hole-0.sketch.wireOp",EDGE,"core_line_2")])]})]});
            var Q73;
            Q73=makeQuery(id+"F5.hole-0.boolean.opBoolean","INTERSECT",EDGE,{"derivedFrom":[makeQuery(id+"F1.opExtrude","SWEPT_FACE",FACE,{"disambiguationData":[OSD([sQuery(id+"F0.wireOp",EDGE,"E0.left")])]}),makeQuery(id+"F5.hole-0.opRevolve","SWEPT_FACE",FACE,{"disambiguationData":[OSD([sQuery(id+"F5.hole-0.sketch.wireOp",EDGE,"core_line_2")])]})]});
            var Q74;
            Q74=makeQuery(id+"F5.hole-0.boolean.opBoolean","INTERSECT",EDGE,{"derivedFrom":[makeQuery(id+"F1.opExtrude","SWEPT_FACE",FACE,{"disambiguationData":[OSD([sQuery(id+"F0.wireOp",EDGE,"E0.left")])]}),makeQuery(id+"F5.hole-0.opRevolve","SWEPT_FACE",FACE,{"disambiguationData":[OSD([sQuery(id+"F5.hole-0.sketch.wireOp",EDGE,"core_line_2")])]})]});
            var Q75;
            Q75=makeQuery(id+"F5.hole-0.boolean.opBoolean","INTERSECT",EDGE,{"derivedFrom":[makeQuery(id+"F1.opExtrude","SWEPT_FACE",FACE,{"disambiguationData":[OSD([sQuery(id+"F0.wireOp",EDGE,"E0.left")])]}),makeQuery(id+"F5.hole-0.opRevolve","SWEPT_FACE",FACE,{"disambiguationData":[OSD([sQuery(id+"F5.hole-0.sketch.wireOp",EDGE,"core_line_2")])]})]});
            var Q76;
            Q76=makeQuery(id+"F5.hole-0.boolean.opBoolean","INTERSECT",EDGE,{"derivedFrom":[makeQuery(id+"F1.opExtrude","SWEPT_FACE",FACE,{"disambiguationData":[OSD([sQuery(id+"F0.wireOp",EDGE,"E0.left")])]}),makeQuery(id+"F5.hole-0.opRevolve","SWEPT_FACE",FACE,{"disambiguationData":[OSD([sQuery(id+"F5.hole-0.sketch.wireOp",EDGE,"core_line_2")])]})]});
            var Q77;
            Q77=makeQuery(id+"F5.hole-0.boolean.opBoolean","INTERSECT",EDGE,{"derivedFrom":[makeQuery(id+"F1.opExtrude","SWEPT_FACE",FACE,{"disambiguationData":[OSD([sQuery(id+"F0.wireOp",EDGE,"E0.left")])]}),makeQuery(id+"F5.hole-0.opRevolve","SWEPT_FACE",FACE,{"disambiguationData":[OSD([sQuery(id+"F5.hole-0.sketch.wireOp",EDGE,"core_line_2")])]})]});
            var Q78;
            Q78=makeQuery(id+"F5.hole-0.boolean.opBoolean","INTERSECT",EDGE,{"derivedFrom":[makeQuery(id+"F1.opExtrude","SWEPT_FACE",FACE,{"disambiguationData":[OSD([sQuery(id+"F0.wireOp",EDGE,"E0.left")])]}),makeQuery(id+"F5.hole-0.opRevolve","SWEPT_FACE",FACE,{"disambiguationData":[OSD([sQuery(id+"F5.hole-0.sketch.wireOp",EDGE,"core_line_2")])]})]});
            var Q79;
            Q79=makeQuery(id+"F5.hole-0.boolean.opBoolean","INTERSECT",EDGE,{"derivedFrom":[makeQuery(id+"F1.opExtrude","SWEPT_FACE",FACE,{"disambiguationData":[OSD([sQuery(id+"F0.wireOp",EDGE,"E0.left")])]}),makeQuery(id+"F5.hole-0.opRevolve","SWEPT_FACE",FACE,{"disambiguationData":[OSD([sQuery(id+"F5.hole-0.sketch.wireOp",EDGE,"core_line_2")])]})]});
            var Q80;
            Q80=makeQuery(id+"F5.hole-0.boolean.opBoolean","INTERSECT",EDGE,{"derivedFrom":[makeQuery(id+"F1.opExtrude","SWEPT_FACE",FACE,{"disambiguationData":[OSD([sQuery(id+"F0.wireOp",EDGE,"E0.left")])]}),makeQuery(id+"F5.hole-0.opRevolve","SWEPT_FACE",FACE,{"disambiguationData":[OSD([sQuery(id+"F5.hole-0.sketch.wireOp",EDGE,"core_line_2")])]})]});
            var Q81;
            Q81=makeQuery(id+"F5.hole-0.boolean.opBoolean","INTERSECT",EDGE,{"derivedFrom":[makeQuery(id+"F1.opExtrude","SWEPT_FACE",FACE,{"disambiguationData":[OSD([sQuery(id+"F0.wireOp",EDGE,"E0.left")])]}),makeQuery(id+"F5.hole-0.opRevolve","SWEPT_FACE",FACE,{"disambiguationData":[OSD([sQuery(id+"F5.hole-0.sketch.wireOp",EDGE,"core_line_2")])]})]});
            var Q82;
            Q82=makeQuery(id+"F5.hole-0.boolean.opBoolean","INTERSECT",EDGE,{"derivedFrom":[makeQuery(id+"F1.opExtrude","SWEPT_FACE",FACE,{"disambiguationData":[OSD([sQuery(id+"F0.wireOp",EDGE,"E0.left")])]}),makeQuery(id+"F5.hole-0.opRevolve","SWEPT_FACE",FACE,{"disambiguationData":[OSD([sQuery(id+"F5.hole-0.sketch.wireOp",EDGE,"core_line_2")])]})]});
            var Q83;
            Q83=makeQuery(id+"F5.hole-0.boolean.opBoolean","INTERSECT",EDGE,{"derivedFrom":[makeQuery(id+"F1.opExtrude","SWEPT_FACE",FACE,{"disambiguationData":[OSD([sQuery(id+"F0.wireOp",EDGE,"E0.left")])]}),makeQuery(id+"F5.hole-0.opRevolve","SWEPT_FACE",FACE,{"disambiguationData":[OSD([sQuery(id+"F5.hole-0.sketch.wireOp",EDGE,"core_line_2")])]})]});
            var Q84;
            Q84=makeQuery(id+"F5.hole-0.boolean.opBoolean","INTERSECT",EDGE,{"derivedFrom":[makeQuery(id+"F1.opExtrude","SWEPT_FACE",FACE,{"disambiguationData":[OSD([sQuery(id+"F0.wireOp",EDGE,"E0.left")])]}),makeQuery(id+"F5.hole-0.opRevolve","SWEPT_FACE",FACE,{"disambiguationData":[OSD([sQuery(id+"F5.hole-0.sketch.wireOp",EDGE,"core_line_2")])]})]});
            var Q85;
            Q85=makeQuery(id+"F5.hole-0.boolean.opBoolean","INTERSECT",EDGE,{"derivedFrom":[makeQuery(id+"F1.opExtrude","SWEPT_FACE",FACE,{"disambiguationData":[OSD([sQuery(id+"F0.wireOp",EDGE,"E0.left")])]}),makeQuery(id+"F5.hole-0.opRevolve","SWEPT_FACE",FACE,{"disambiguationData":[OSD([sQuery(id+"F5.hole-0.sketch.wireOp",EDGE,"core_line_2")])]})]});
            var Q86;
            Q86=makeQuery(id+"F5.hole-0.boolean.opBoolean","INTERSECT",EDGE,{"derivedFrom":[makeQuery(id+"F1.opExtrude","SWEPT_FACE",FACE,{"disambiguationData":[OSD([sQuery(id+"F0.wireOp",EDGE,"E0.left")])]}),makeQuery(id+"F5.hole-0.opRevolve","SWEPT_FACE",FACE,{"disambiguationData":[OSD([sQuery(id+"F5.hole-0.sketch.wireOp",EDGE,"core_line_2")])]})]});
            var Q87;
            Q87=makeQuery(id+"F5.hole-0.boolean.opBoolean","INTERSECT",EDGE,{"derivedFrom":[makeQuery(id+"F1.opExtrude","SWEPT_FACE",FACE,{"disambiguationData":[OSD([sQuery(id+"F0.wireOp",EDGE,"E0.left")])]}),makeQuery(id+"F5.hole-0.opRevolve","SWEPT_FACE",FACE,{"disambiguationData":[OSD([sQuery(id+"F5.hole-0.sketch.wireOp",EDGE,"core_line_2")])]})]});
            var Q88;
            Q88=makeQuery(id+"F5.hole-0.boolean.opBoolean","INTERSECT",EDGE,{"derivedFrom":[makeQuery(id+"F1.opExtrude","SWEPT_FACE",FACE,{"disambiguationData":[OSD([sQuery(id+"F0.wireOp",EDGE,"E0.left")])]}),makeQuery(id+"F5.hole-0.opRevolve","SWEPT_FACE",FACE,{"disambiguationData":[OSD([sQuery(id+"F5.hole-0.sketch.wireOp",EDGE,"core_line_2")])]})]});
            var Q89;
            Q89=makeQuery(id+"F5.hole-0.boolean.opBoolean","INTERSECT",EDGE,{"derivedFrom":[makeQuery(id+"F1.opExtrude","SWEPT_FACE",FACE,{"disambiguationData":[OSD([sQuery(id+"F0.wireOp",EDGE,"E0.left")])]}),makeQuery(id+"F5.hole-0.opRevolve","SWEPT_FACE",FACE,{"disambiguationData":[OSD([sQuery(id+"F5.hole-0.sketch.wireOp",EDGE,"core_line_2")])]})]});
            var Q90;
            Q90=makeQuery(id+"F5.hole-0.boolean.opBoolean","INTERSECT",EDGE,{"derivedFrom":[makeQuery(id+"F1.opExtrude","SWEPT_FACE",FACE,{"disambiguationData":[OSD([sQuery(id+"F0.wireOp",EDGE,"E0.left")])]}),makeQuery(id+"F5.hole-0.opRevolve","SWEPT_FACE",FACE,{"disambiguationData":[OSD([sQuery(id+"F5.hole-0.sketch.wireOp",EDGE,"core_line_2")])]})]});
            var Q91;
            Q91=makeQuery(id+"F5.hole-0.boolean.opBoolean","INTERSECT",EDGE,{"derivedFrom":[makeQuery(id+"F1.opExtrude","SWEPT_FACE",FACE,{"disambiguationData":[OSD([sQuery(id+"F0.wireOp",EDGE,"E0.left")])]}),makeQuery(id+"F5.hole-0.opRevolve","SWEPT_FACE",FACE,{"disambiguationData":[OSD([sQuery(id+"F5.hole-0.sketch.wireOp",EDGE,"core_line_2")])]})]});
            var Q92;
            Q92=makeQuery(id+"F7.hole-0.boolean.opBoolean","COPY",FACE,{"disambiguationData":[TD([makeQuery(id+"F1.opExtrude","SWEPT_FACE",FACE,{"disambiguationData":[OSD([sQuery(id+"F0.wireOp",EDGE,"E0.top")])]})])],"derivedFrom":makeQuery(id+"F7.hole-0.opRevolve","SWEPT_FACE",FACE,{"disambiguationData":[OSD([sQuery(id+"F7.hole-0.sketch.wireOp",EDGE,"core_line_2")])]})});
            var Q93;
            {var subQ0=makeQuery(id+"F3.hole-0.boolean.opBoolean","COPY",FACE,{"derivedFrom":makeQuery(id+"F3.hole-0.opRevolve","SWEPT_FACE",FACE,{"disambiguationData":[OSD([sQuery(id+"F3.hole-0.sketch.wireOp",EDGE,"core_line_2")])]})});Q93=makeQuery(id+"F5.hole-0.boolean.opBoolean","SPLIT",FACE,{"disambiguationData":[TD([makeQuery(id+"F1.opExtrude","CAP_FACE",FACE,{"disambiguationData":[OSD([sQuery(id+"F0.wireOp",EDGE,"E0.bottom"),sQuery(id+"F0.wireOp",EDGE,"E0.top"),sQuery(id+"F0.wireOp",EDGE,"E0.left"),sQuery(id+"F0.wireOp",EDGE,"E0.right")])],"isStart":true})])],"derivedFrom":subQ0});}
            var Q94;
            Q94=makeQuery(id+"F7.hole-0.boolean.opBoolean","COPY",FACE,{"disambiguationData":[TD([makeQuery(id+"F1.opExtrude","SWEPT_FACE",FACE,{"disambiguationData":[OSD([sQuery(id+"F0.wireOp",EDGE,"E0.bottom")])]})])],"derivedFrom":makeQuery(id+"F7.hole-0.opRevolve","SWEPT_FACE",FACE,{"disambiguationData":[OSD([sQuery(id+"F7.hole-0.sketch.wireOp",EDGE,"core_line_2")])]})});
            var Q95;
            Q95=makeQuery(id+"F3.hole-0.boolean.opBoolean","COPY",EDGE,{"derivedFrom":makeQuery(id+"F3.hole-0.opRevolve","SWEPT_EDGE",EDGE,{"disambiguationData":[OSD([sQuery(id+"F3.hole-0.sketch.wireOp",EDGE,"core_line_2"),sQuery(id+"F3.hole-0.sketch.wireOp",EDGE,"core_line_3")])]})});
            var Q96;
            Q96=makeQuery(id+"F3.hole-0.boolean.opBoolean","COPY",EDGE,{"derivedFrom":makeQuery(id+"F3.hole-0.opRevolve","SWEPT_EDGE",EDGE,{"disambiguationData":[OSD([sQuery(id+"F3.hole-0.sketch.wireOp",EDGE,"core_line_2"),sQuery(id+"F3.hole-0.sketch.wireOp",EDGE,"core_line_3")])]})});
            var Q97;
            Q97=makeQuery(id+"F3.hole-0.boolean.opBoolean","COPY",EDGE,{"derivedFrom":makeQuery(id+"F3.hole-0.opRevolve","SWEPT_EDGE",EDGE,{"disambiguationData":[OSD([sQuery(id+"F3.hole-0.sketch.wireOp",EDGE,"core_line_2"),sQuery(id+"F3.hole-0.sketch.wireOp",EDGE,"core_line_3")])]})});
            var Q98;
            Q98=makeQuery(id+"F3.hole-0.boolean.opBoolean","COPY",EDGE,{"derivedFrom":makeQuery(id+"F3.hole-0.opRevolve","SWEPT_EDGE",EDGE,{"disambiguationData":[OSD([sQuery(id+"F3.hole-0.sketch.wireOp",EDGE,"core_line_2"),sQuery(id+"F3.hole-0.sketch.wireOp",EDGE,"core_line_3")])]})});
            var Q99;
            Q99=makeQuery(id+"F3.hole-0.boolean.opBoolean","COPY",EDGE,{"derivedFrom":makeQuery(id+"F3.hole-0.opRevolve","SWEPT_EDGE",EDGE,{"disambiguationData":[OSD([sQuery(id+"F3.hole-0.sketch.wireOp",EDGE,"core_line_2"),sQuery(id+"F3.hole-0.sketch.wireOp",EDGE,"core_line_3")])]})});
            var Q100;
            Q100=makeQuery(id+"F3.hole-0.boolean.opBoolean","COPY",EDGE,{"derivedFrom":makeQuery(id+"F3.hole-0.opRevolve","SWEPT_EDGE",EDGE,{"disambiguationData":[OSD([sQuery(id+"F3.hole-0.sketch.wireOp",EDGE,"core_line_2"),sQuery(id+"F3.hole-0.sketch.wireOp",EDGE,"core_line_3")])]})});
            var Q101;
            Q101=makeQuery(id+"F3.hole-0.boolean.opBoolean","COPY",EDGE,{"derivedFrom":makeQuery(id+"F3.hole-0.opRevolve","SWEPT_EDGE",EDGE,{"disambiguationData":[OSD([sQuery(id+"F3.hole-0.sketch.wireOp",EDGE,"core_line_2"),sQuery(id+"F3.hole-0.sketch.wireOp",EDGE,"core_line_3")])]})});
            var Q102;
            Q102=makeQuery(id+"F3.hole-0.boolean.opBoolean","COPY",EDGE,{"derivedFrom":makeQuery(id+"F3.hole-0.opRevolve","SWEPT_EDGE",EDGE,{"disambiguationData":[OSD([sQuery(id+"F3.hole-0.sketch.wireOp",EDGE,"core_line_2"),sQuery(id+"F3.hole-0.sketch.wireOp",EDGE,"core_line_3")])]})});
            var Q103;
            Q103=makeQuery(id+"F3.hole-0.boolean.opBoolean","COPY",EDGE,{"derivedFrom":makeQuery(id+"F3.hole-0.opRevolve","SWEPT_EDGE",EDGE,{"disambiguationData":[OSD([sQuery(id+"F3.hole-0.sketch.wireOp",EDGE,"core_line_2"),sQuery(id+"F3.hole-0.sketch.wireOp",EDGE,"core_line_3")])]})});
            var Q104;
            Q104=makeQuery(id+"F3.hole-0.boolean.opBoolean","COPY",EDGE,{"derivedFrom":makeQuery(id+"F3.hole-0.opRevolve","SWEPT_EDGE",EDGE,{"disambiguationData":[OSD([sQuery(id+"F3.hole-0.sketch.wireOp",EDGE,"core_line_2"),sQuery(id+"F3.hole-0.sketch.wireOp",EDGE,"core_line_3")])]})});
            var Q105;
            Q105=makeQuery(id+"F3.hole-0.boolean.opBoolean","COPY",EDGE,{"derivedFrom":makeQuery(id+"F3.hole-0.opRevolve","SWEPT_EDGE",EDGE,{"disambiguationData":[OSD([sQuery(id+"F3.hole-0.sketch.wireOp",EDGE,"core_line_2"),sQuery(id+"F3.hole-0.sketch.wireOp",EDGE,"core_line_3")])]})});
            var Q106;
            Q106=makeQuery(id+"F3.hole-0.boolean.opBoolean","COPY",EDGE,{"derivedFrom":makeQuery(id+"F3.hole-0.opRevolve","SWEPT_EDGE",EDGE,{"disambiguationData":[OSD([sQuery(id+"F3.hole-0.sketch.wireOp",EDGE,"core_line_2"),sQuery(id+"F3.hole-0.sketch.wireOp",EDGE,"core_line_3")])]})});
            var Q107;
            Q107=makeQuery(id+"F3.hole-0.boolean.opBoolean","COPY",EDGE,{"derivedFrom":makeQuery(id+"F3.hole-0.opRevolve","SWEPT_EDGE",EDGE,{"disambiguationData":[OSD([sQuery(id+"F3.hole-0.sketch.wireOp",EDGE,"core_line_2"),sQuery(id+"F3.hole-0.sketch.wireOp",EDGE,"core_line_3")])]})});
            var Q108;
            Q108=makeQuery(id+"F3.hole-0.boolean.opBoolean","COPY",EDGE,{"derivedFrom":makeQuery(id+"F3.hole-0.opRevolve","SWEPT_EDGE",EDGE,{"disambiguationData":[OSD([sQuery(id+"F3.hole-0.sketch.wireOp",EDGE,"core_line_2"),sQuery(id+"F3.hole-0.sketch.wireOp",EDGE,"core_line_3")])]})});
            var Q109;
            Q109=makeQuery(id+"F3.hole-0.boolean.opBoolean","COPY",EDGE,{"derivedFrom":makeQuery(id+"F3.hole-0.opRevolve","SWEPT_EDGE",EDGE,{"disambiguationData":[OSD([sQuery(id+"F3.hole-0.sketch.wireOp",EDGE,"core_line_2"),sQuery(id+"F3.hole-0.sketch.wireOp",EDGE,"core_line_3")])]})});
            var Q110;
            Q110=makeQuery(id+"F3.hole-0.boolean.opBoolean","COPY",EDGE,{"derivedFrom":makeQuery(id+"F3.hole-0.opRevolve","SWEPT_EDGE",EDGE,{"disambiguationData":[OSD([sQuery(id+"F3.hole-0.sketch.wireOp",EDGE,"core_line_2"),sQuery(id+"F3.hole-0.sketch.wireOp",EDGE,"core_line_3")])]})});
            var Q111;
            Q111=makeQuery(id+"F3.hole-0.boolean.opBoolean","COPY",EDGE,{"derivedFrom":makeQuery(id+"F3.hole-0.opRevolve","SWEPT_EDGE",EDGE,{"disambiguationData":[OSD([sQuery(id+"F3.hole-0.sketch.wireOp",EDGE,"core_line_2"),sQuery(id+"F3.hole-0.sketch.wireOp",EDGE,"core_line_3")])]})});
            var Q112;
            Q112=makeQuery(id+"F3.hole-0.boolean.opBoolean","COPY",EDGE,{"derivedFrom":makeQuery(id+"F3.hole-0.opRevolve","SWEPT_EDGE",EDGE,{"disambiguationData":[OSD([sQuery(id+"F3.hole-0.sketch.wireOp",EDGE,"core_line_2"),sQuery(id+"F3.hole-0.sketch.wireOp",EDGE,"core_line_3")])]})});
            var Q113;
            Q113=makeQuery(id+"F3.hole-0.boolean.opBoolean","COPY",EDGE,{"derivedFrom":makeQuery(id+"F3.hole-0.opRevolve","SWEPT_EDGE",EDGE,{"disambiguationData":[OSD([sQuery(id+"F3.hole-0.sketch.wireOp",EDGE,"core_line_2"),sQuery(id+"F3.hole-0.sketch.wireOp",EDGE,"core_line_3")])]})});
            var Q114;
            Q114=makeQuery(id+"F3.hole-0.boolean.opBoolean","COPY",EDGE,{"derivedFrom":makeQuery(id+"F3.hole-0.opRevolve","SWEPT_EDGE",EDGE,{"disambiguationData":[OSD([sQuery(id+"F3.hole-0.sketch.wireOp",EDGE,"core_line_2"),sQuery(id+"F3.hole-0.sketch.wireOp",EDGE,"core_line_3")])]})});
            var Q115;
            Q115=makeQuery(id+"F3.hole-0.boolean.opBoolean","COPY",EDGE,{"derivedFrom":makeQuery(id+"F3.hole-0.opRevolve","SWEPT_EDGE",EDGE,{"disambiguationData":[OSD([sQuery(id+"F3.hole-0.sketch.wireOp",EDGE,"core_line_2"),sQuery(id+"F3.hole-0.sketch.wireOp",EDGE,"core_line_3")])]})});
            var Q116;
            Q116=makeQuery(id+"F3.hole-0.boolean.opBoolean","COPY",EDGE,{"derivedFrom":makeQuery(id+"F3.hole-0.opRevolve","SWEPT_EDGE",EDGE,{"disambiguationData":[OSD([sQuery(id+"F3.hole-0.sketch.wireOp",EDGE,"core_line_2"),sQuery(id+"F3.hole-0.sketch.wireOp",EDGE,"core_line_3")])]})});
            var Q117;
            Q117=makeQuery(id+"F3.hole-0.boolean.opBoolean","COPY",EDGE,{"derivedFrom":makeQuery(id+"F3.hole-0.opRevolve","SWEPT_EDGE",EDGE,{"disambiguationData":[OSD([sQuery(id+"F3.hole-0.sketch.wireOp",EDGE,"core_line_2"),sQuery(id+"F3.hole-0.sketch.wireOp",EDGE,"core_line_3")])]})});
            var Q118;
            Q118=makeQuery(id+"F3.hole-0.boolean.opBoolean","COPY",EDGE,{"derivedFrom":makeQuery(id+"F3.hole-0.opRevolve","SWEPT_EDGE",EDGE,{"disambiguationData":[OSD([sQuery(id+"F3.hole-0.sketch.wireOp",EDGE,"core_line_2"),sQuery(id+"F3.hole-0.sketch.wireOp",EDGE,"core_line_3")])]})});
            var Q119;
            Q119=makeQuery(id+"F3.hole-0.boolean.opBoolean","COPY",EDGE,{"derivedFrom":makeQuery(id+"F3.hole-0.opRevolve","SWEPT_EDGE",EDGE,{"disambiguationData":[OSD([sQuery(id+"F3.hole-0.sketch.wireOp",EDGE,"core_line_2"),sQuery(id+"F3.hole-0.sketch.wireOp",EDGE,"core_line_3")])]})});
            var Q120;
            Q120=makeQuery(id+"F3.hole-0.boolean.opBoolean","COPY",EDGE,{"derivedFrom":makeQuery(id+"F3.hole-0.opRevolve","SWEPT_EDGE",EDGE,{"disambiguationData":[OSD([sQuery(id+"F3.hole-0.sketch.wireOp",EDGE,"core_line_2"),sQuery(id+"F3.hole-0.sketch.wireOp",EDGE,"core_line_3")])]})});
            var Q121;
            Q121=makeQuery(id+"F3.hole-0.boolean.opBoolean","COPY",EDGE,{"derivedFrom":makeQuery(id+"F3.hole-0.opRevolve","SWEPT_EDGE",EDGE,{"disambiguationData":[OSD([sQuery(id+"F3.hole-0.sketch.wireOp",EDGE,"core_line_2"),sQuery(id+"F3.hole-0.sketch.wireOp",EDGE,"core_line_3")])]})});
            var Q122;
            Q122=makeQuery(id+"F3.hole-0.boolean.opBoolean","COPY",EDGE,{"derivedFrom":makeQuery(id+"F3.hole-0.opRevolve","SWEPT_EDGE",EDGE,{"disambiguationData":[OSD([sQuery(id+"F3.hole-0.sketch.wireOp",EDGE,"core_line_2"),sQuery(id+"F3.hole-0.sketch.wireOp",EDGE,"core_line_3")])]})});
            var Q123;
            Q123=makeQuery(id+"F3.hole-0.boolean.opBoolean","COPY",EDGE,{"derivedFrom":makeQuery(id+"F3.hole-0.opRevolve","SWEPT_EDGE",EDGE,{"disambiguationData":[OSD([sQuery(id+"F3.hole-0.sketch.wireOp",EDGE,"core_line_2"),sQuery(id+"F3.hole-0.sketch.wireOp",EDGE,"core_line_3")])]})});
            var Q124;
            Q124=makeQuery(id+"F3.hole-0.boolean.opBoolean","COPY",EDGE,{"derivedFrom":makeQuery(id+"F3.hole-0.opRevolve","SWEPT_EDGE",EDGE,{"disambiguationData":[OSD([sQuery(id+"F3.hole-0.sketch.wireOp",EDGE,"core_line_2"),sQuery(id+"F3.hole-0.sketch.wireOp",EDGE,"core_line_3")])]})});
            var Q125;
            Q125=makeQuery(id+"F3.hole-0.boolean.opBoolean","COPY",EDGE,{"derivedFrom":makeQuery(id+"F3.hole-0.opRevolve","SWEPT_EDGE",EDGE,{"disambiguationData":[OSD([sQuery(id+"F3.hole-0.sketch.wireOp",EDGE,"core_line_2"),sQuery(id+"F3.hole-0.sketch.wireOp",EDGE,"core_line_3")])]})});
            var Q126;
            Q126=makeQuery(id+"F3.hole-0.boolean.opBoolean","COPY",EDGE,{"derivedFrom":makeQuery(id+"F3.hole-0.opRevolve","SWEPT_EDGE",EDGE,{"disambiguationData":[OSD([sQuery(id+"F3.hole-0.sketch.wireOp",EDGE,"core_line_2"),sQuery(id+"F3.hole-0.sketch.wireOp",EDGE,"core_line_3")])]})});
            var Q127;
            Q127=makeQuery(id+"F3.hole-0.boolean.opBoolean","COPY",EDGE,{"derivedFrom":makeQuery(id+"F3.hole-0.opRevolve","SWEPT_EDGE",EDGE,{"disambiguationData":[OSD([sQuery(id+"F3.hole-0.sketch.wireOp",EDGE,"core_line_2"),sQuery(id+"F3.hole-0.sketch.wireOp",EDGE,"core_line_3")])]})});
            var Q128;
            Q128=makeQuery(id+"F3.hole-0.boolean.opBoolean","COPY",EDGE,{"derivedFrom":makeQuery(id+"F3.hole-0.opRevolve","SWEPT_EDGE",EDGE,{"disambiguationData":[OSD([sQuery(id+"F3.hole-0.sketch.wireOp",EDGE,"core_line_2"),sQuery(id+"F3.hole-0.sketch.wireOp",EDGE,"core_line_3")])]})});
            var Q129;
            Q129=makeQuery(id+"F3.hole-0.boolean.opBoolean","COPY",EDGE,{"derivedFrom":makeQuery(id+"F3.hole-0.opRevolve","SWEPT_EDGE",EDGE,{"disambiguationData":[OSD([sQuery(id+"F3.hole-0.sketch.wireOp",EDGE,"core_line_2"),sQuery(id+"F3.hole-0.sketch.wireOp",EDGE,"core_line_3")])]})});
            var Q130;
            Q130=makeQuery(id+"F3.hole-0.boolean.opBoolean","COPY",EDGE,{"derivedFrom":makeQuery(id+"F3.hole-0.opRevolve","SWEPT_EDGE",EDGE,{"disambiguationData":[OSD([sQuery(id+"F3.hole-0.sketch.wireOp",EDGE,"core_line_2"),sQuery(id+"F3.hole-0.sketch.wireOp",EDGE,"core_line_3")])]})});
            var Q131;
            Q131=makeQuery(id+"F3.hole-0.boolean.opBoolean","COPY",EDGE,{"derivedFrom":makeQuery(id+"F3.hole-0.opRevolve","SWEPT_EDGE",EDGE,{"disambiguationData":[OSD([sQuery(id+"F3.hole-0.sketch.wireOp",EDGE,"core_line_2"),sQuery(id+"F3.hole-0.sketch.wireOp",EDGE,"core_line_3")])]})});
            var Q132;
            Q132=makeQuery(id+"F3.hole-0.boolean.opBoolean","COPY",EDGE,{"derivedFrom":makeQuery(id+"F3.hole-0.opRevolve","SWEPT_EDGE",EDGE,{"disambiguationData":[OSD([sQuery(id+"F3.hole-0.sketch.wireOp",EDGE,"core_line_2"),sQuery(id+"F3.hole-0.sketch.wireOp",EDGE,"core_line_3")])]})});
            var Q133;
            Q133=makeQuery(id+"F3.hole-0.boolean.opBoolean","COPY",EDGE,{"derivedFrom":makeQuery(id+"F3.hole-0.opRevolve","SWEPT_EDGE",EDGE,{"disambiguationData":[OSD([sQuery(id+"F3.hole-0.sketch.wireOp",EDGE,"core_line_2"),sQuery(id+"F3.hole-0.sketch.wireOp",EDGE,"core_line_3")])]})});
            var Q134;
            Q134=makeQuery(id+"F3.hole-0.boolean.opBoolean","COPY",EDGE,{"derivedFrom":makeQuery(id+"F3.hole-0.opRevolve","SWEPT_EDGE",EDGE,{"disambiguationData":[OSD([sQuery(id+"F3.hole-0.sketch.wireOp",EDGE,"core_line_2"),sQuery(id+"F3.hole-0.sketch.wireOp",EDGE,"core_line_3")])]})});
            var Q135;
            Q135=makeQuery(id+"F3.hole-0.boolean.opBoolean","COPY",EDGE,{"derivedFrom":makeQuery(id+"F3.hole-0.opRevolve","SWEPT_EDGE",EDGE,{"disambiguationData":[OSD([sQuery(id+"F3.hole-0.sketch.wireOp",EDGE,"core_line_2"),sQuery(id+"F3.hole-0.sketch.wireOp",EDGE,"core_line_3")])]})});
            var Q136;
            Q136=makeQuery(id+"F3.hole-0.boolean.opBoolean","COPY",EDGE,{"derivedFrom":makeQuery(id+"F3.hole-0.opRevolve","SWEPT_EDGE",EDGE,{"disambiguationData":[OSD([sQuery(id+"F3.hole-0.sketch.wireOp",EDGE,"core_line_2"),sQuery(id+"F3.hole-0.sketch.wireOp",EDGE,"core_line_3")])]})});
            var Q137;
            Q137=makeQuery(id+"F3.hole-0.boolean.opBoolean","COPY",EDGE,{"derivedFrom":makeQuery(id+"F3.hole-0.opRevolve","SWEPT_EDGE",EDGE,{"disambiguationData":[OSD([sQuery(id+"F3.hole-0.sketch.wireOp",EDGE,"core_line_2"),sQuery(id+"F3.hole-0.sketch.wireOp",EDGE,"core_line_3")])]})});
            var Q138;
            Q138=makeQuery(id+"F3.hole-0.boolean.opBoolean","COPY",EDGE,{"derivedFrom":makeQuery(id+"F3.hole-0.opRevolve","SWEPT_EDGE",EDGE,{"disambiguationData":[OSD([sQuery(id+"F3.hole-0.sketch.wireOp",EDGE,"core_line_2"),sQuery(id+"F3.hole-0.sketch.wireOp",EDGE,"core_line_3")])]})});
            var Q139;
            Q139=makeQuery(id+"F3.hole-0.boolean.opBoolean","COPY",EDGE,{"derivedFrom":makeQuery(id+"F3.hole-0.opRevolve","SWEPT_EDGE",EDGE,{"disambiguationData":[OSD([sQuery(id+"F3.hole-0.sketch.wireOp",EDGE,"core_line_2"),sQuery(id+"F3.hole-0.sketch.wireOp",EDGE,"core_line_3")])]})});
            var Q140;
            Q140=makeQuery(id+"F3.hole-0.boolean.opBoolean","COPY",EDGE,{"derivedFrom":makeQuery(id+"F3.hole-0.opRevolve","SWEPT_EDGE",EDGE,{"disambiguationData":[OSD([sQuery(id+"F3.hole-0.sketch.wireOp",EDGE,"core_line_2"),sQuery(id+"F3.hole-0.sketch.wireOp",EDGE,"core_line_3")])]})});
            var Q141;
            Q141=makeQuery(id+"F3.hole-0.boolean.opBoolean","COPY",EDGE,{"derivedFrom":makeQuery(id+"F3.hole-0.opRevolve","SWEPT_EDGE",EDGE,{"disambiguationData":[OSD([sQuery(id+"F3.hole-0.sketch.wireOp",EDGE,"core_line_2"),sQuery(id+"F3.hole-0.sketch.wireOp",EDGE,"core_line_3")])]})});
            var Q142;
            Q142=makeQuery(id+"F3.hole-0.boolean.opBoolean","COPY",EDGE,{"derivedFrom":makeQuery(id+"F3.hole-0.opRevolve","SWEPT_EDGE",EDGE,{"disambiguationData":[OSD([sQuery(id+"F3.hole-0.sketch.wireOp",EDGE,"core_line_2"),sQuery(id+"F3.hole-0.sketch.wireOp",EDGE,"core_line_3")])]})});
            var Q143;
            Q143=makeQuery(id+"F3.hole-0.boolean.opBoolean","COPY",EDGE,{"derivedFrom":makeQuery(id+"F3.hole-0.opRevolve","SWEPT_EDGE",EDGE,{"disambiguationData":[OSD([sQuery(id+"F3.hole-0.sketch.wireOp",EDGE,"core_line_2"),sQuery(id+"F3.hole-0.sketch.wireOp",EDGE,"core_line_3")])]})});
            var Q144;
            Q144=makeQuery(id+"F3.hole-0.boolean.opBoolean","COPY",EDGE,{"derivedFrom":makeQuery(id+"F3.hole-0.opRevolve","SWEPT_EDGE",EDGE,{"disambiguationData":[OSD([sQuery(id+"F3.hole-0.sketch.wireOp",EDGE,"core_line_2"),sQuery(id+"F3.hole-0.sketch.wireOp",EDGE,"core_line_3")])]})});
            var Q145;
            Q145=makeQuery(id+"F3.hole-0.boolean.opBoolean","COPY",EDGE,{"derivedFrom":makeQuery(id+"F3.hole-0.opRevolve","SWEPT_EDGE",EDGE,{"disambiguationData":[OSD([sQuery(id+"F3.hole-0.sketch.wireOp",EDGE,"core_line_2"),sQuery(id+"F3.hole-0.sketch.wireOp",EDGE,"core_line_3")])]})});
            var Q146;
            Q146=makeQuery(id+"F3.hole-0.boolean.opBoolean","COPY",EDGE,{"derivedFrom":makeQuery(id+"F3.hole-0.opRevolve","SWEPT_EDGE",EDGE,{"disambiguationData":[OSD([sQuery(id+"F3.hole-0.sketch.wireOp",EDGE,"core_line_2"),sQuery(id+"F3.hole-0.sketch.wireOp",EDGE,"core_line_3")])]})});
            var Q147;
            Q147=makeQuery(id+"F3.hole-0.boolean.opBoolean","COPY",EDGE,{"derivedFrom":makeQuery(id+"F3.hole-0.opRevolve","SWEPT_EDGE",EDGE,{"disambiguationData":[OSD([sQuery(id+"F3.hole-0.sketch.wireOp",EDGE,"core_line_2"),sQuery(id+"F3.hole-0.sketch.wireOp",EDGE,"core_line_3")])]})});
            var Q148;
            Q148=makeQuery(id+"F3.hole-0.boolean.opBoolean","COPY",EDGE,{"derivedFrom":makeQuery(id+"F3.hole-0.opRevolve","SWEPT_EDGE",EDGE,{"disambiguationData":[OSD([sQuery(id+"F3.hole-0.sketch.wireOp",EDGE,"core_line_2"),sQuery(id+"F3.hole-0.sketch.wireOp",EDGE,"core_line_3")])]})});
            var Q149;
            Q149=makeQuery(id+"F3.hole-0.boolean.opBoolean","COPY",EDGE,{"derivedFrom":makeQuery(id+"F3.hole-0.opRevolve","SWEPT_EDGE",EDGE,{"disambiguationData":[OSD([sQuery(id+"F3.hole-0.sketch.wireOp",EDGE,"core_line_2"),sQuery(id+"F3.hole-0.sketch.wireOp",EDGE,"core_line_3")])]})});
            var Q150;
            Q150=makeQuery(id+"F3.hole-0.boolean.opBoolean","COPY",EDGE,{"derivedFrom":makeQuery(id+"F3.hole-0.opRevolve","SWEPT_EDGE",EDGE,{"disambiguationData":[OSD([sQuery(id+"F3.hole-0.sketch.wireOp",EDGE,"core_line_2"),sQuery(id+"F3.hole-0.sketch.wireOp",EDGE,"core_line_3")])]})});
            var Q151;
            Q151=makeQuery(id+"F3.hole-0.boolean.opBoolean","COPY",EDGE,{"derivedFrom":makeQuery(id+"F3.hole-0.opRevolve","SWEPT_EDGE",EDGE,{"disambiguationData":[OSD([sQuery(id+"F3.hole-0.sketch.wireOp",EDGE,"core_line_2"),sQuery(id+"F3.hole-0.sketch.wireOp",EDGE,"core_line_3")])]})});
            var Q152;
            Q152=makeQuery(id+"F3.hole-0.boolean.opBoolean","COPY",EDGE,{"derivedFrom":makeQuery(id+"F3.hole-0.opRevolve","SWEPT_EDGE",EDGE,{"disambiguationData":[OSD([sQuery(id+"F3.hole-0.sketch.wireOp",EDGE,"core_line_2"),sQuery(id+"F3.hole-0.sketch.wireOp",EDGE,"core_line_3")])]})});
            var Q153;
            Q153=makeQuery(id+"F3.hole-0.boolean.opBoolean","COPY",EDGE,{"derivedFrom":makeQuery(id+"F3.hole-0.opRevolve","SWEPT_EDGE",EDGE,{"disambiguationData":[OSD([sQuery(id+"F3.hole-0.sketch.wireOp",EDGE,"core_line_2"),sQuery(id+"F3.hole-0.sketch.wireOp",EDGE,"core_line_3")])]})});
            var Q154;
            Q154=makeQuery(id+"F3.hole-0.boolean.opBoolean","COPY",EDGE,{"derivedFrom":makeQuery(id+"F3.hole-0.opRevolve","SWEPT_EDGE",EDGE,{"disambiguationData":[OSD([sQuery(id+"F3.hole-0.sketch.wireOp",EDGE,"core_line_2"),sQuery(id+"F3.hole-0.sketch.wireOp",EDGE,"core_line_3")])]})});
            var Q155;
            Q155=makeQuery(id+"F3.hole-0.boolean.opBoolean","COPY",EDGE,{"derivedFrom":makeQuery(id+"F3.hole-0.opRevolve","SWEPT_EDGE",EDGE,{"disambiguationData":[OSD([sQuery(id+"F3.hole-0.sketch.wireOp",EDGE,"core_line_2"),sQuery(id+"F3.hole-0.sketch.wireOp",EDGE,"core_line_3")])]})});
            var Q156;
            Q156=makeQuery(id+"F3.hole-0.boolean.opBoolean","COPY",EDGE,{"derivedFrom":makeQuery(id+"F3.hole-0.opRevolve","SWEPT_EDGE",EDGE,{"disambiguationData":[OSD([sQuery(id+"F3.hole-0.sketch.wireOp",EDGE,"core_line_2"),sQuery(id+"F3.hole-0.sketch.wireOp",EDGE,"core_line_3")])]})});
            var Q157;
            Q157=makeQuery(id+"F3.hole-0.boolean.opBoolean","COPY",EDGE,{"derivedFrom":makeQuery(id+"F3.hole-0.opRevolve","SWEPT_EDGE",EDGE,{"disambiguationData":[OSD([sQuery(id+"F3.hole-0.sketch.wireOp",EDGE,"core_line_2"),sQuery(id+"F3.hole-0.sketch.wireOp",EDGE,"core_line_3")])]})});
            var Q158;
            Q158=makeQuery(id+"F3.hole-0.boolean.opBoolean","COPY",EDGE,{"derivedFrom":makeQuery(id+"F3.hole-0.opRevolve","SWEPT_EDGE",EDGE,{"disambiguationData":[OSD([sQuery(id+"F3.hole-0.sketch.wireOp",EDGE,"core_line_2"),sQuery(id+"F3.hole-0.sketch.wireOp",EDGE,"core_line_3")])]})});
            var Q159;
            {var subQ0=makeQuery(id+"F3.hole-0.boolean.opBoolean","COPY",FACE,{"derivedFrom":makeQuery(id+"F3.hole-0.opRevolve","SWEPT_FACE",FACE,{"disambiguationData":[OSD([sQuery(id+"F3.hole-0.sketch.wireOp",EDGE,"core_line_2")])]})});Q159=makeQuery(id+"F5.hole-0.boolean.opBoolean","SPLIT",FACE,{"disambiguationData":[TD([makeQuery(id+"F1.opExtrude","CAP_FACE",FACE,{"disambiguationData":[OSD([sQuery(id+"F0.wireOp",EDGE,"E0.bottom"),sQuery(id+"F0.wireOp",EDGE,"E0.top"),sQuery(id+"F0.wireOp",EDGE,"E0.left"),sQuery(id+"F0.wireOp",EDGE,"E0.right")])],"isStart":false})])],"derivedFrom":subQ0});}
            var Q160;
            Q160=makeQuery(id+"F8.opFillet","SPLIT",FACE,{"disambiguationData":[OD(3.0)],"derivedFrom":makeQuery(id+"F1.opExtrude","SWEPT_FACE",FACE,{"disambiguationData":[OSD([sQuery(id+"F0.wireOp",EDGE,"E0.left")])]})});
            var Q161;
            Q161=makeQuery(id+"F5.hole-0.boolean.opBoolean","COPY",EDGE,{"derivedFrom":makeQuery(id+"F5.hole-0.opRevolve","SWEPT_EDGE",EDGE,{"disambiguationData":[OSD([sQuery(id+"F5.hole-0.sketch.wireOp",EDGE,"core_line_2"),sQuery(id+"F5.hole-0.sketch.wireOp",EDGE,"core_line_3")])]})});
            var Q162;
            Q162=makeQuery(id+"F5.hole-0.boolean.opBoolean","COPY",EDGE,{"derivedFrom":makeQuery(id+"F5.hole-0.opRevolve","SWEPT_EDGE",EDGE,{"disambiguationData":[OSD([sQuery(id+"F5.hole-0.sketch.wireOp",EDGE,"core_line_2"),sQuery(id+"F5.hole-0.sketch.wireOp",EDGE,"core_line_3")])]})});
            var Q163;
            Q163=makeQuery(id+"F5.hole-0.boolean.opBoolean","COPY",EDGE,{"derivedFrom":makeQuery(id+"F5.hole-0.opRevolve","SWEPT_EDGE",EDGE,{"disambiguationData":[OSD([sQuery(id+"F5.hole-0.sketch.wireOp",EDGE,"core_line_2"),sQuery(id+"F5.hole-0.sketch.wireOp",EDGE,"core_line_3")])]})});
            var Q164;
            Q164=makeQuery(id+"F5.hole-0.boolean.opBoolean","COPY",EDGE,{"derivedFrom":makeQuery(id+"F5.hole-0.opRevolve","SWEPT_EDGE",EDGE,{"disambiguationData":[OSD([sQuery(id+"F5.hole-0.sketch.wireOp",EDGE,"core_line_2"),sQuery(id+"F5.hole-0.sketch.wireOp",EDGE,"core_line_3")])]})});
            var Q165;
            Q165=makeQuery(id+"F5.hole-0.boolean.opBoolean","COPY",EDGE,{"derivedFrom":makeQuery(id+"F5.hole-0.opRevolve","SWEPT_EDGE",EDGE,{"disambiguationData":[OSD([sQuery(id+"F5.hole-0.sketch.wireOp",EDGE,"core_line_2"),sQuery(id+"F5.hole-0.sketch.wireOp",EDGE,"core_line_3")])]})});
            var Q166;
            Q166=makeQuery(id+"F5.hole-0.boolean.opBoolean","COPY",EDGE,{"derivedFrom":makeQuery(id+"F5.hole-0.opRevolve","SWEPT_EDGE",EDGE,{"disambiguationData":[OSD([sQuery(id+"F5.hole-0.sketch.wireOp",EDGE,"core_line_2"),sQuery(id+"F5.hole-0.sketch.wireOp",EDGE,"core_line_3")])]})});
            var Q167;
            Q167=makeQuery(id+"F5.hole-0.boolean.opBoolean","COPY",EDGE,{"derivedFrom":makeQuery(id+"F5.hole-0.opRevolve","SWEPT_EDGE",EDGE,{"disambiguationData":[OSD([sQuery(id+"F5.hole-0.sketch.wireOp",EDGE,"core_line_2"),sQuery(id+"F5.hole-0.sketch.wireOp",EDGE,"core_line_3")])]})});
            var Q168;
            Q168=makeQuery(id+"F5.hole-0.boolean.opBoolean","COPY",EDGE,{"derivedFrom":makeQuery(id+"F5.hole-0.opRevolve","SWEPT_EDGE",EDGE,{"disambiguationData":[OSD([sQuery(id+"F5.hole-0.sketch.wireOp",EDGE,"core_line_2"),sQuery(id+"F5.hole-0.sketch.wireOp",EDGE,"core_line_3")])]})});
            var Q169;
            {var subQ0=sQuery(id+"F0.wireOp",EDGE,"E0.right");Q169=makeQuery(id+"F8.opFillet","BLEND_EDGE",EDGE,{"disambiguationData":[OD(0.0)],"blendedFrom":[makeQuery(id+"F1.opExtrude","CAP_EDGE",EDGE,{"disambiguationData":[OSD([subQ0])],"isStart":false}),makeQuery(id+"F1.opExtrude","CAP_FACE",FACE,{"disambiguationData":[OSD([sQuery(id+"F0.wireOp",EDGE,"E0.bottom"),sQuery(id+"F0.wireOp",EDGE,"E0.top"),sQuery(id+"F0.wireOp",EDGE,"E0.left"),subQ0])],"isStart":false})],"blendedInto":[makeQuery(id+"F1.opExtrude","CAP_FACE",FACE,{"disambiguationData":[OSD([sQuery(id+"F0.wireOp",EDGE,"E0.bottom"),sQuery(id+"F0.wireOp",EDGE,"E0.top"),sQuery(id+"F0.wireOp",EDGE,"E0.left"),subQ0])],"isStart":false})]});}
            var Q170;
            {var subQ0=sQuery(id+"F0.wireOp",EDGE,"E0.bottom");Q170=makeQuery(id+"F8.opFillet","BLEND_EDGE",EDGE,{"disambiguationData":[OD(0.0)],"blendedFrom":[makeQuery(id+"F1.opExtrude","CAP_EDGE",EDGE,{"disambiguationData":[OSD([subQ0])],"isStart":false}),makeQuery(id+"F1.opExtrude","CAP_FACE",FACE,{"disambiguationData":[OSD([subQ0,sQuery(id+"F0.wireOp",EDGE,"E0.top"),sQuery(id+"F0.wireOp",EDGE,"E0.left"),sQuery(id+"F0.wireOp",EDGE,"E0.right")])],"isStart":false})],"blendedInto":[makeQuery(id+"F1.opExtrude","CAP_FACE",FACE,{"disambiguationData":[OSD([subQ0,sQuery(id+"F0.wireOp",EDGE,"E0.top"),sQuery(id+"F0.wireOp",EDGE,"E0.left"),sQuery(id+"F0.wireOp",EDGE,"E0.right")])],"isStart":false})]});}
            var Q171;
            {var subQ0=sQuery(id+"F0.wireOp",EDGE,"E0.left");Q171=makeQuery(id+"F8.opFillet","BLEND_EDGE",EDGE,{"disambiguationData":[OD(0.0)],"blendedFrom":[makeQuery(id+"F1.opExtrude","SWEPT_EDGE",EDGE,{"disambiguationData":[OSD([sQuery(id+"F0.wireOp",EDGE,"E0.bottom"),subQ0])]}),makeQuery(id+"F1.opExtrude","SWEPT_FACE",FACE,{"disambiguationData":[OSD([subQ0])]})],"blendedInto":[makeQuery(id+"F1.opExtrude","SWEPT_FACE",FACE,{"disambiguationData":[OSD([subQ0])]})]});}
            var Q172;
            {var subQ0=sQuery(id+"F0.wireOp",EDGE,"E0.left");Q172=makeQuery(id+"F8.opFillet","BLEND_FACE",FACE,{"disambiguationData":[OSD([subQ0]),TDD([makeQuery(id+"F1.opExtrude","CAP_EDGE",EDGE,{"disambiguationData":[OSD([subQ0])],"isStart":true})])]});}
            var Q173;
            {var subQ0=sQuery(id+"F0.wireOp",EDGE,"E0.left");Q173=makeQuery(id+"F8.opFillet","BLEND_EDGE",EDGE,{"disambiguationData":[OD(0.0)],"blendedFrom":[makeQuery(id+"F1.opExtrude","CAP_EDGE",EDGE,{"disambiguationData":[OSD([subQ0])],"isStart":true}),makeQuery(id+"F1.opExtrude","SWEPT_FACE",FACE,{"disambiguationData":[OSD([subQ0])]})],"blendedInto":[makeQuery(id+"F1.opExtrude","SWEPT_FACE",FACE,{"disambiguationData":[OSD([subQ0])]})]});}
            var Q174;
            {var subQ0=sQuery(id+"F0.wireOp",EDGE,"E0.left");Q174=makeQuery(id+"F8.opFillet","BLEND_EDGE",EDGE,{"disambiguationData":[OD(1.0)],"blendedFrom":[makeQuery(id+"F1.opExtrude","CAP_EDGE",EDGE,{"disambiguationData":[OSD([subQ0])],"isStart":true}),makeQuery(id+"F1.opExtrude","SWEPT_FACE",FACE,{"disambiguationData":[OSD([subQ0])]})],"blendedInto":[makeQuery(id+"F1.opExtrude","SWEPT_FACE",FACE,{"disambiguationData":[OSD([subQ0])]})]});}
            var Q175;
            {var subQ0=sQuery(id+"F0.wireOp",EDGE,"E0.left");Q175=makeQuery(id+"F8.opFillet","BLEND_EDGE",EDGE,{"disambiguationData":[OD(0.0)],"blendedFrom":[makeQuery(id+"F1.opExtrude","SWEPT_EDGE",EDGE,{"disambiguationData":[OSD([sQuery(id+"F0.wireOp",EDGE,"E0.top"),subQ0])]}),makeQuery(id+"F1.opExtrude","SWEPT_FACE",FACE,{"disambiguationData":[OSD([subQ0])]})],"blendedInto":[makeQuery(id+"F1.opExtrude","SWEPT_FACE",FACE,{"disambiguationData":[OSD([subQ0])]})]});}
            var Q176;
            {var subQ0=sQuery(id+"F0.wireOp",EDGE,"E0.left");Q176=makeQuery(id+"F8.opFillet","BLEND_EDGE",EDGE,{"disambiguationData":[OD(1.0)],"blendedFrom":[makeQuery(id+"F1.opExtrude","SWEPT_EDGE",EDGE,{"disambiguationData":[OSD([sQuery(id+"F0.wireOp",EDGE,"E0.top"),subQ0])]}),makeQuery(id+"F1.opExtrude","SWEPT_FACE",FACE,{"disambiguationData":[OSD([subQ0])]})],"blendedInto":[makeQuery(id+"F1.opExtrude","SWEPT_FACE",FACE,{"disambiguationData":[OSD([subQ0])]})]});}
            var Q177;
            {var subQ0=sQuery(id+"F0.wireOp",EDGE,"E0.left");Q177=makeQuery(id+"F8.opFillet","BLEND_EDGE",EDGE,{"disambiguationData":[OD(1.0)],"blendedFrom":[makeQuery(id+"F1.opExtrude","CAP_EDGE",EDGE,{"disambiguationData":[OSD([subQ0])],"isStart":false}),makeQuery(id+"F1.opExtrude","SWEPT_FACE",FACE,{"disambiguationData":[OSD([subQ0])]})],"blendedInto":[makeQuery(id+"F1.opExtrude","SWEPT_FACE",FACE,{"disambiguationData":[OSD([subQ0])]})]});}
            var Q178;
            {var subQ0=sQuery(id+"F0.wireOp",EDGE,"E0.left");Q178=makeQuery(id+"F8.opFillet","BLEND_EDGE",EDGE,{"disambiguationData":[OD(0.0)],"blendedFrom":[makeQuery(id+"F1.opExtrude","CAP_EDGE",EDGE,{"disambiguationData":[OSD([subQ0])],"isStart":false}),makeQuery(id+"F1.opExtrude","SWEPT_FACE",FACE,{"disambiguationData":[OSD([subQ0])]})],"blendedInto":[makeQuery(id+"F1.opExtrude","SWEPT_FACE",FACE,{"disambiguationData":[OSD([subQ0])]})]});}
            var Q179;
            {var subQ0=sQuery(id+"F0.wireOp",EDGE,"E0.left");Q179=makeQuery(id+"F8.opFillet","BLEND_EDGE",EDGE,{"disambiguationData":[OD(1.0)],"blendedFrom":[makeQuery(id+"F1.opExtrude","SWEPT_EDGE",EDGE,{"disambiguationData":[OSD([sQuery(id+"F0.wireOp",EDGE,"E0.bottom"),subQ0])]}),makeQuery(id+"F1.opExtrude","SWEPT_FACE",FACE,{"disambiguationData":[OSD([subQ0])]})],"blendedInto":[makeQuery(id+"F1.opExtrude","SWEPT_FACE",FACE,{"disambiguationData":[OSD([subQ0])]})]});}
            fillet(context, id + "F9", {"entities" : qUnion([Q0, Q1, Q2, Q3, Q4, Q5, Q6, Q7, Q8, Q9, Q10, Q11, Q12, Q13, Q14, Q15, Q16, Q17, Q18, Q19, Q20, Q21, Q22, Q23, Q24, Q25, Q26, Q27, Q28, Q29, Q30, Q31, Q32, Q33, Q34, Q35, Q36, Q37, Q38, Q39, Q40, Q41, Q42, Q43, Q44, Q45, Q46, Q47, Q48, Q49, Q50, Q51, Q52, Q53, Q54, Q55, Q56, Q57, Q58, Q59, Q60, Q61, Q62, Q63, Q64, Q65, Q66, Q67, Q68, Q69, Q70, Q71, Q72, Q73, Q74, Q75, Q76, Q77, Q78, Q79, Q80, Q81, Q82, Q83, Q84, Q85, Q86, Q87, Q88, Q89, Q90, Q91, Q92, Q93, Q94, Q95, Q96, Q97, Q98, Q99, Q100, Q101, Q102, Q103, Q104, Q105, Q106, Q107, Q108, Q109, Q110, Q111, Q112, Q113, Q114, Q115, Q116, Q117, Q118, Q119, Q120, Q121, Q122, Q123, Q124, Q125, Q126, Q127, Q128, Q129, Q130, Q131, Q132, Q133, Q134, Q135, Q136, Q137, Q138, Q139, Q140, Q141, Q142, Q143, Q144, Q145, Q146, Q147, Q148, Q149, Q150, Q151, Q152, Q153, Q154, Q155, Q156, Q157, Q158, Q159, Q160, Q161, Q162, Q163, Q164, Q165, Q166, Q167, Q168, Q169, Q170, Q171, Q172, Q173, Q174, Q175, Q176, Q177, Q178, Q179]), "radius" : 5 * mm, "tangentPropagation" : true, "allowEdgeOverflow" : false});
        }
    });
